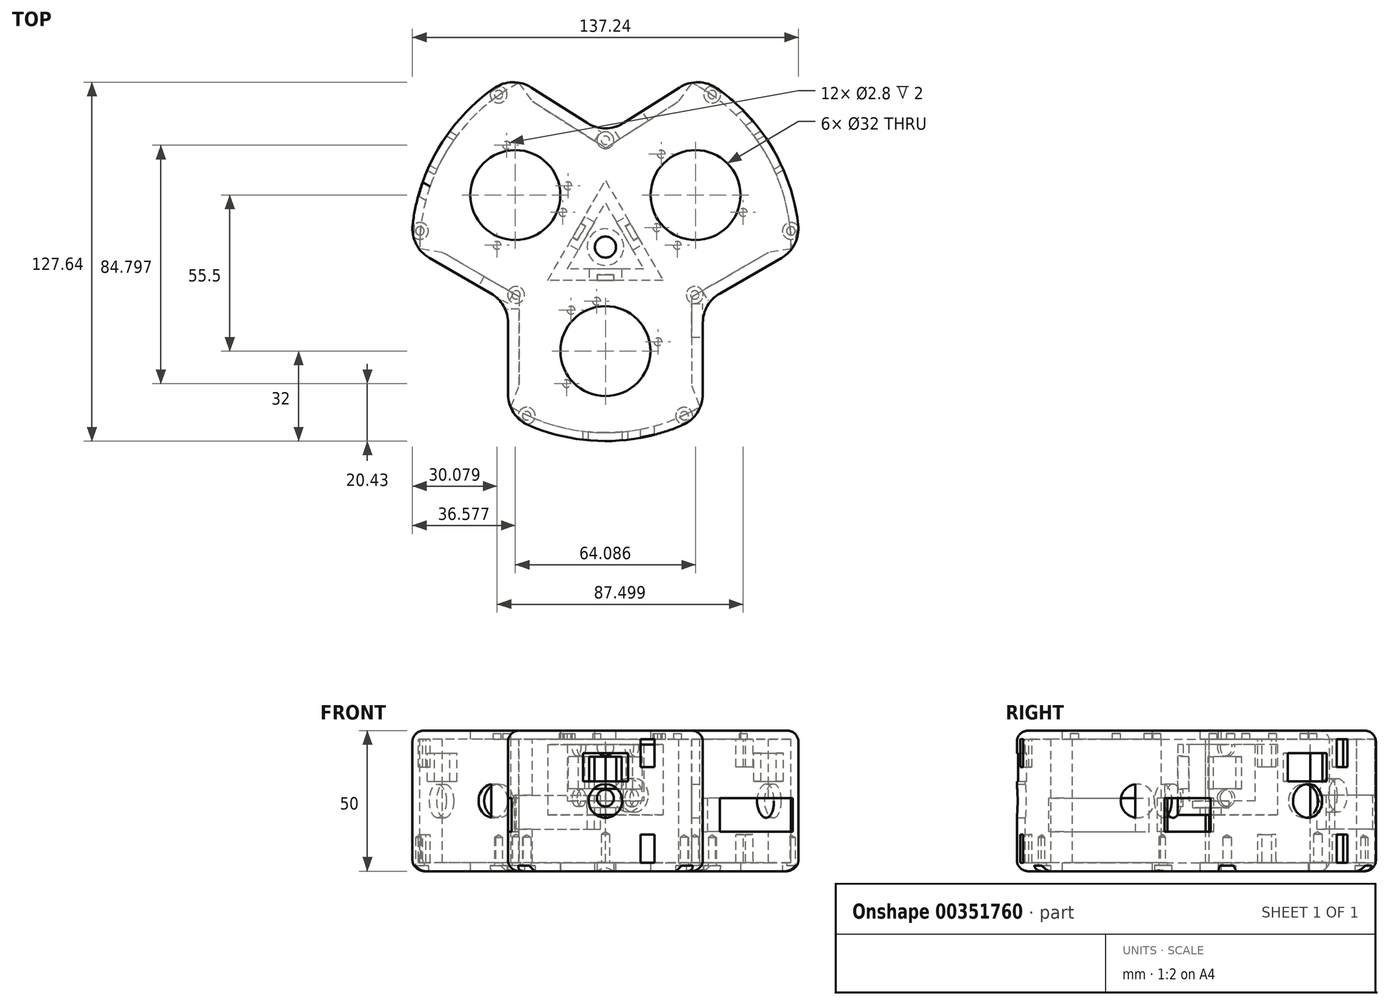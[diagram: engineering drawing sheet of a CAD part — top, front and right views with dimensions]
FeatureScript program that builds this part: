
annotation { "Feature Type Name" : "Feature", "Feature Type Description" : "" }
export const myFeature = defineFeature(function(context is Context, id is Id, definition is map)
    precondition{}
    {
        {
            var Q0;
            Q0=qCreatedBy(makeId("Top.planeOp"),FACE);
            var sketch = newSketch(context, id + "F0", { "sketchPlane" : qUnion([Q0])});
            skCircle(sketch, "E0.cCircle", {"center": v(0, 0) * mm, "radius": 7.84 * mm, "construction": true});
            skLineSegment(sketch, "E0.0", {"start": v(13.57, -7.84) * mm, "end": v(-13.57, -7.84) * mm});
            skLineSegment(sketch, "E0.1", {"start": v(-13.57, -7.84) * mm, "end": v(0, 15.67) * mm});
            skLineSegment(sketch, "E0.2", {"start": v(0, 15.67) * mm, "end": v(13.57, -7.84) * mm});
            skPoint(sketch, "E0.0.midPoint", {"position": v(0, -7.84) * mm});
            skLineSegment(sketch, "E1.0", {"start": v(-20.5, -11.84) * mm, "end": v(0, 23.67) * mm});
            skLineSegment(sketch, "E1.1", {"start": v(20.5, -11.84) * mm, "end": v(-20.5, -11.84) * mm});
            skLineSegment(sketch, "E1.2", {"start": v(0, 23.67) * mm, "end": v(20.5, -11.84) * mm});
            skCircle(sketch, "E2", {"center": v(0, 0) * mm, "radius": 3.25 * mm});
            skSolve(sketch);
        }
        {
            var Q0;
            Q0 = qSketchRegion(id + "F0", true);
            extrude(context, id + "F1", {"entities" : qUnion([Q0]), "depth" : 20 * mm, "offsetDistance" : 25 * mm});
        }
        {
            var Q0;
            Q0=makeQuery(id+"F0.imprint","IMPRINT",FACE,{"disambiguationData":[TD([[makeQuery(id+"F0.imprint","IMPRINT",EDGE,{"derivedFrom":sQuery(id+"F0.wireOp",EDGE,"E0.0")}),-1.0]])]});
            var Q1;
            Q1=makeQuery(id+"F0.imprint","IMPRINT",FACE,{"disambiguationData":[TD([[makeQuery(id+"F0.imprint","IMPRINT",EDGE,{"derivedFrom":sQuery(id+"F0.wireOp",EDGE,"E0.0")}),1.0]])]});
            var Q2;
            Q2=makeQuery(id+"F0.imprint","IMPRINT",FACE,{"disambiguationData":[TD([[makeQuery(id+"F0.imprint","IMPRINT",EDGE,{"derivedFrom":sQuery(id+"F0.wireOp",EDGE,"E2")}),1.0]])]});
            extrude(context, id + "F2", {"entities" : qUnion([Q0, Q1, Q2]), "operationType" : NewBodyOperationType.ADD, "oppositeDirection" : true, "depth" : 5 * mm, "offsetDistance" : 25 * mm});
        }
        {
            var Q0;
            {var subQ0=sQuery(id+"F0.wireOp",EDGE,"E1.1");Q0=makeQuery(id+"F2.boolean.opBoolean","MERGE",FACE,{"derivedFrom":[makeQuery(id+"F1.opExtrude","SWEPT_FACE",FACE,{"disambiguationData":[OSD([subQ0])]}),makeQuery(id+"F2.opExtrude","SWEPT_FACE",FACE,{"disambiguationData":[OSD([subQ0])]})]});}
            var sketch = newSketch(context, id + "F3", { "sketchPlane" : qUnion([Q0])});
            skLineSegment(sketch, "E3.bottom", {"start": v(5.75, 4.25) * mm, "end": v(-5.75, 4.25) * mm});
            skLineSegment(sketch, "E3.top", {"start": v(5.75, 15.75) * mm, "end": v(-5.75, 15.75) * mm});
            skLineSegment(sketch, "E3.left", {"start": v(5.75, 4.25) * mm, "end": v(5.75, 15.75) * mm});
            skLineSegment(sketch, "E3.right", {"start": v(-5.75, 4.25) * mm, "end": v(-5.75, 15.75) * mm});
            skPoint(sketch, "E3.middle", {"position": v(0, 10) * mm});
            skCircle(sketch, "E4", {"center": v(0, 10) * mm, "radius": 3.25 * mm});
            skCircle(sketch, "E5", {"center": v(0, 19) * mm, "radius": 3 * mm});
            skPoint(sketch, "E5.centerSnap0", {"position": v(0, 20) * mm});
            skCircle(sketch, "E6", {"center": v(0, 1) * mm, "radius": 3 * mm});
            skPoint(sketch, "E6.centerSnap0", {"position": v(0, 4.25) * mm});
            skSolve(sketch);
        }
        {
            var Q0;
            {var subQ0=sQuery(id+"F0.wireOp",EDGE,"E1.2");Q0=makeQuery(id+"F2.boolean.opBoolean","MERGE",FACE,{"derivedFrom":[makeQuery(id+"F1.opExtrude","SWEPT_FACE",FACE,{"disambiguationData":[OSD([subQ0])]}),makeQuery(id+"F2.opExtrude","SWEPT_FACE",FACE,{"disambiguationData":[OSD([subQ0])]})]});}
            var sketch = newSketch(context, id + "F4", { "sketchPlane" : qUnion([Q0])});
            skLineSegment(sketch, "E7.bottom", {"start": v(5.75, 4.25) * mm, "end": v(-5.75, 4.25) * mm});
            skLineSegment(sketch, "E7.top", {"start": v(5.75, 15.75) * mm, "end": v(-5.75, 15.75) * mm});
            skLineSegment(sketch, "E7.left", {"start": v(5.75, 4.25) * mm, "end": v(5.75, 15.75) * mm});
            skLineSegment(sketch, "E7.right", {"start": v(-5.75, 4.25) * mm, "end": v(-5.75, 15.75) * mm});
            skPoint(sketch, "E7.middle", {"position": v(0, 10) * mm});
            skCircle(sketch, "E8", {"center": v(0, 10) * mm, "radius": 3.25 * mm});
            skCircle(sketch, "E9", {"center": v(0, 19) * mm, "radius": 3 * mm});
            skPoint(sketch, "E9.centerSnap0", {"position": v(0, 15.75) * mm});
            skCircle(sketch, "E10", {"center": v(0, 1) * mm, "radius": 3 * mm});
            skSolve(sketch);
        }
        {
            var Q0;
            {var subQ0=sQuery(id+"F0.wireOp",EDGE,"E1.0");Q0=makeQuery(id+"F2.boolean.opBoolean","MERGE",FACE,{"derivedFrom":[makeQuery(id+"F1.opExtrude","SWEPT_FACE",FACE,{"disambiguationData":[OSD([subQ0])]}),makeQuery(id+"F2.opExtrude","SWEPT_FACE",FACE,{"disambiguationData":[OSD([subQ0])]})]});}
            var sketch = newSketch(context, id + "F5", { "sketchPlane" : qUnion([Q0])});
            skLineSegment(sketch, "E11.bottom", {"start": v(-5.75, 4.25) * mm, "end": v(5.75, 4.25) * mm});
            skLineSegment(sketch, "E11.top", {"start": v(-5.75, 15.75) * mm, "end": v(5.75, 15.75) * mm});
            skLineSegment(sketch, "E11.left", {"start": v(-5.75, 4.25) * mm, "end": v(-5.75, 15.75) * mm});
            skLineSegment(sketch, "E11.right", {"start": v(5.75, 4.25) * mm, "end": v(5.75, 15.75) * mm});
            skPoint(sketch, "E11.middle", {"position": v(0, 10) * mm});
            skCircle(sketch, "E12", {"center": v(0, 10) * mm, "radius": 3.25 * mm});
            skCircle(sketch, "E13", {"center": v(0, 19) * mm, "radius": 3 * mm});
            skPoint(sketch, "E13.centerSnap0", {"position": v(0, 15.75) * mm});
            skCircle(sketch, "E14", {"center": v(0, 1) * mm, "radius": 3 * mm});
            skPoint(sketch, "E14.centerSnap0", {"position": v(0, 4.25) * mm});
            skSolve(sketch);
        }
        {
            var Q0;
            Q0=makeQuery(id+"F5.imprint","IMPRINT",FACE,{"disambiguationData":[TD([[makeQuery(id+"F5.imprint","IMPRINT",EDGE,{"derivedFrom":sQuery(id+"F5.wireOp",EDGE,"E11.bottom")}),1.0]])]});
            extrude(context, id + "F6", {"entities" : qUnion([Q0]), "operationType" : NewBodyOperationType.REMOVE, "oppositeDirection" : true, "depth" : 7.4 * mm, "offsetDistance" : 25 * mm});
        }
        {
            var Q0;
            Q0=makeQuery(id+"F4.imprint","IMPRINT",FACE,{"disambiguationData":[TD([[makeQuery(id+"F4.imprint","IMPRINT",EDGE,{"derivedFrom":sQuery(id+"F4.wireOp",EDGE,"E7.bottom")}),-1.0]])]});
            var Q1;
            Q1=makeQuery(id+"F4.imprint","IMPRINT",FACE,{"disambiguationData":[TD([[makeQuery(id+"F4.imprint","IMPRINT",EDGE,{"derivedFrom":sQuery(id+"F4.wireOp",EDGE,"E8")}),1.0]])]});
            extrude(context, id + "F7", {"entities" : qUnion([Q0, Q1]), "operationType" : NewBodyOperationType.REMOVE, "oppositeDirection" : true, "depth" : 7.5 * mm, "offsetDistance" : 25 * mm});
        }
        {
            var Q0;
            Q0=makeQuery(id+"F3.imprint","IMPRINT",FACE,{"disambiguationData":[TD([[makeQuery(id+"F3.imprint","IMPRINT",EDGE,{"derivedFrom":sQuery(id+"F3.wireOp",EDGE,"E3.bottom")}),-1.0]])]});
            extrude(context, id + "F8", {"entities" : qUnion([Q0]), "operationType" : NewBodyOperationType.REMOVE, "oppositeDirection" : true, "depth" : 6.4 * mm, "offsetDistance" : 25 * mm});
        }
        {
            var Q0;
            Q0=makeQuery(id+"F5.imprint","IMPRINT",FACE,{"disambiguationData":[TD([[makeQuery(id+"F5.imprint","IMPRINT",EDGE,{"derivedFrom":sQuery(id+"F5.wireOp",EDGE,"E12")}),1.0]])]});
            extrude(context, id + "F9", {"entities" : qUnion([Q0]), "operationType" : NewBodyOperationType.REMOVE, "oppositeDirection" : true, "depth" : 5 * mm, "offsetDistance" : 25 * mm});
        }
        {
            var Q0;
            Q0=makeQuery(id+"F3.imprint","IMPRINT",FACE,{"disambiguationData":[TD([[makeQuery(id+"F3.imprint","IMPRINT",EDGE,{"derivedFrom":sQuery(id+"F3.wireOp",EDGE,"E4")}),1.0]])]});
            extrude(context, id + "F10", {"entities" : qUnion([Q0]), "operationType" : NewBodyOperationType.REMOVE, "oppositeDirection" : true, "depth" : 5 * mm, "offsetDistance" : 25 * mm});
        }
        {
            var Q0;
            Q0=makeQuery(id+"F4.imprint","IMPRINT",FACE,{"disambiguationData":[TD([[makeQuery(id+"F4.imprint","IMPRINT",EDGE,{"derivedFrom":sQuery(id+"F4.wireOp",EDGE,"E8")}),1.0]])]});
            extrude(context, id + "F11", {"entities" : qUnion([Q0]), "operationType" : NewBodyOperationType.REMOVE, "oppositeDirection" : true, "depth" : 5 * mm, "offsetDistance" : 25 * mm});
        }
        {
            var Q0;
            Q0=sQuery(id+"F0.wireOp",VERTEX,"E0.cCircle.center");
            var Q1;
            Q1=makeQuery(id+"F1.opExtrude","SWEPT_BODY",BODY,{"disambiguationData":[OSD([sQuery(id+"F0.wireOp",EDGE,"E0.0"),sQuery(id+"F0.wireOp",EDGE,"E0.1"),sQuery(id+"F0.wireOp",EDGE,"E0.2"),sQuery(id+"F0.wireOp",EDGE,"E1.0"),sQuery(id+"F0.wireOp",EDGE,"E1.1"),sQuery(id+"F0.wireOp",EDGE,"E1.2")])]});
            hole(context, id + "F12", {"style" : HoleStyle.C_BORE, "endStyle" : HoleEndStyle.BLIND, "holeDiameter" : 6.5 * mm, "cBoreDiameter" : 13 * mm, "cBoreDepth" : 2.5 * mm, "majorDiameter" : 5 * mm, "holeDepth" : 12 * mm, "isTappedThrough" : true, "tappedDepth" : 12 * mm, "tapClearance" : 3, "locations" : qUnion([Q0]), "scope" : qUnion([Q1])});
        }
        {
            var Q0;
            Q0=qCreatedBy(makeId("Front.planeOp"),FACE);
            var sketch = newSketch(context, id + "F13", { "sketchPlane" : qUnion([Q0])});
            skLineSegment(sketch, "E15.bottom", {"start": v(0, -22) * mm, "end": v(-66, -22) * mm});
            skLineSegment(sketch, "E15.top", {"start": v(0, 22) * mm, "end": v(-66, 22) * mm});
            skLineSegment(sketch, "E15.right", {"start": v(-66, -22) * mm, "end": v(-66, 22) * mm});
            skPoint(sketch, "E15.middle", {"position": v(-33, 0) * mm});
            skLineSegment(sketch, "E16.0", {"start": v(0, -25) * mm, "end": v(-69, -25) * mm});
            skLineSegment(sketch, "E16.1", {"start": v(-69, -25) * mm, "end": v(-69, 25) * mm});
            skLineSegment(sketch, "E16.2", {"start": v(0, 25) * mm, "end": v(-69, 25) * mm});
            skLineSegment(sketch, "E17", {"start": v(0, 25) * mm, "end": v(0, 22) * mm});
            skLineSegment(sketch, "E18", {"start": v(0, -22) * mm, "end": v(0, -25) * mm});
            skLineSegment(sketch, "E19", {"start": v(-66, -22) * mm, "end": v(-69, -22) * mm});
            skSolve(sketch);
        }
        {
            var Q0;
            Q0=makeQuery(id+"F13.imprint","IMPRINT",FACE,{"disambiguationData":[TD([[makeQuery(id+"F13.imprint","IMPRINT",EDGE,{"derivedFrom":sQuery(id+"F13.wireOp",EDGE,"E15.top")}),-1.0]])]});
            var Q1;
            Q1=sQuery(id+"F13.wireOp",EDGE,"E17");
            revolve(context, id + "F14", {"entities" : qUnion([Q0]), "axis" : qUnion([Q1]), "revolveType" : RevolveType.FULL, "surfaceOperationType" : NewSurfaceOperationType.NEW});
        }
        {
            var Q0;
            Q0=makeQuery(id+"F13.imprint","IMPRINT",FACE,{"disambiguationData":[TD([[makeQuery(id+"F13.imprint","IMPRINT",EDGE,{"derivedFrom":sQuery(id+"F13.wireOp",EDGE,"E15.bottom")}),1.0]])]});
            var Q1;
            Q1=sQuery(id+"F13.wireOp",EDGE,"E18");
            revolve(context, id + "F15", {"surfaceOperationType" : NewSurfaceOperationType.NEW, "entities" : qUnion([Q0]), "axis" : qUnion([Q1]), "revolveType" : RevolveType.FULL});
        }
        {
            var Q0;
            Q0=qCreatedBy(makeId("Top.planeOp"),FACE);
            var sketch = newSketch(context, id + "F16", { "sketchPlane" : qUnion([Q0])});
            skCircle(sketch, "E20", {"center": v(0, -37) * mm, "radius": 16 * mm});
            skLineSegment(sketch, "E21", {"start": v(48.46, 27.98) * mm, "end": v(0, 0) * mm, "construction": true});
            skLineSegment(sketch, "E22", {"start": v(0, 0) * mm, "end": v(-43.02, 24.84) * mm, "construction": true});
            skCircle(sketch, "E23", {"center": v(32.04, 18.5) * mm, "radius": 16 * mm});
            skCircle(sketch, "E24", {"center": v(-32.04, 18.5) * mm, "radius": 16 * mm});
            skCircle(sketch, "E25", {"center": v(0, 0) * mm, "radius": 3.25 * mm});
            skSolve(sketch);
        }
        {
            var Q0;
            Q0=makeQuery(id+"F16.imprint","IMPRINT",FACE,{"disambiguationData":[TD([[makeQuery(id+"F16.imprint","IMPRINT",EDGE,{"derivedFrom":sQuery(id+"F16.wireOp",EDGE,"E24")}),1.0]])]});
            var Q1;
            Q1=makeQuery(id+"F16.imprint","IMPRINT",FACE,{"disambiguationData":[TD([[makeQuery(id+"F16.imprint","IMPRINT",EDGE,{"derivedFrom":sQuery(id+"F16.wireOp",EDGE,"E23")}),1.0]])]});
            var Q2;
            Q2=makeQuery(id+"F16.imprint","IMPRINT",FACE,{"disambiguationData":[TD([[makeQuery(id+"F16.imprint","IMPRINT",EDGE,{"derivedFrom":sQuery(id+"F16.wireOp",EDGE,"E20")}),1.0]])]});
            extrude(context, id + "F17", {"entities" : qUnion([Q0, Q1, Q2]), "operationType" : NewBodyOperationType.REMOVE, "depth" : 64 * mm, "offsetDistance" : 25 * mm, "hasSecondDirection" : true, "secondDirectionOppositeDirection" : true, "secondDirectionDepth" : 43 * mm});
        }
        {
            var Q0;
            Q0=qCreatedBy(makeId("Front.planeOp"),FACE);
            var sketch = newSketch(context, id + "F18", { "sketchPlane" : qUnion([Q0])});
            skLineSegment(sketch, "E26.bottom", {"start": v(8, 7) * mm, "end": v(-8, 7) * mm});
            skLineSegment(sketch, "E26.top", {"start": v(8, 17) * mm, "end": v(-8, 17) * mm});
            skLineSegment(sketch, "E26.left", {"start": v(8, 7) * mm, "end": v(8, 17) * mm});
            skLineSegment(sketch, "E26.right", {"start": v(-8, 7) * mm, "end": v(-8, 17) * mm});
            skPoint(sketch, "E26.middle", {"position": v(0, 12) * mm});
            skCircle(sketch, "E27", {"center": v(0, 0) * mm, "radius": 6 * mm});
            skLineSegment(sketch, "E28.bottom", {"start": v(17.5, 12) * mm, "end": v(12.5, 12) * mm});
            skLineSegment(sketch, "E28.top", {"start": v(17.5, 22) * mm, "end": v(12.5, 22) * mm});
            skLineSegment(sketch, "E28.left", {"start": v(17.5, 12) * mm, "end": v(17.5, 22) * mm});
            skLineSegment(sketch, "E28.right", {"start": v(12.5, 12) * mm, "end": v(12.5, 22) * mm});
            skPoint(sketch, "E28.middle", {"position": v(15, 17) * mm});
            skLineSegment(sketch, "E29.bottom", {"start": v(17.5, -22) * mm, "end": v(12.5, -22) * mm});
            skLineSegment(sketch, "E29.top", {"start": v(17.5, -12) * mm, "end": v(12.5, -12) * mm});
            skLineSegment(sketch, "E29.left", {"start": v(17.5, -22) * mm, "end": v(17.5, -12) * mm});
            skLineSegment(sketch, "E29.right", {"start": v(12.5, -22) * mm, "end": v(12.5, -12) * mm});
            skPoint(sketch, "E29.middle", {"position": v(15, -17) * mm});
            skPoint(sketch, "E29.cornerSnap0", {"position": v(17.5, 17) * mm});
            skSolve(sketch);
        }
        {
            var Q0;
            Q0 = qSketchRegion(id + "F18", true);
            extrude(context, id + "F19", {"entities" : qUnion([Q0]), "operationType" : NewBodyOperationType.REMOVE, "depth" : 101.5 * mm, "offsetDistance" : 25 * mm, "hasSecondDirection" : true, "secondDirectionOppositeDirection" : false, "secondDirectionDepth" : 60 * mm});
        }
        {
            var Q0;
            {var subQ0=sQuery(id+"F0.wireOp",EDGE,"E1.2");var subQ1=sQuery(id+"F0.wireOp",EDGE,"E1.1");Q0=makeQuery(id+"F2.boolean.opBoolean","MERGE",EDGE,{"derivedFrom":[makeQuery(id+"F1.opExtrude","SWEPT_EDGE",EDGE,{"disambiguationData":[OSD([subQ1,subQ0])]}),makeQuery(id+"F2.opExtrude","SWEPT_EDGE",EDGE,{"disambiguationData":[OSD([subQ1,subQ0])]})]});}
            cPlane(context, id + "F20", {"entities" : qUnion([Q0]), "cplaneType" : CPlaneType.LINE_ANGLE, "offset" : 134 * mm, "angle" : 30 * degree, "width" : 150 * mm, "height" : 150 * mm});
        }
        {
            var Q0;
            {var subQ0=sQuery(id+"F0.wireOp",EDGE,"E1.1");var subQ1=sQuery(id+"F0.wireOp",EDGE,"E1.0");Q0=makeQuery(id+"F2.boolean.opBoolean","MERGE",EDGE,{"derivedFrom":[makeQuery(id+"F1.opExtrude","SWEPT_EDGE",EDGE,{"disambiguationData":[OSD([subQ1,subQ0])]}),makeQuery(id+"F2.opExtrude","SWEPT_EDGE",EDGE,{"disambiguationData":[OSD([subQ1,subQ0])]})]});}
            cPlane(context, id + "F21", {"entities" : qUnion([Q0]), "cplaneType" : CPlaneType.LINE_ANGLE, "offset" : 25 * mm, "angle" : 30 * degree, "oppositeDirection" : true, "width" : 150 * mm, "height" : 150 * mm});
        }
        {
            var Q0;
            Q0=qCreatedBy(id+"F21.planeOp",FACE);
            var sketch = newSketch(context, id + "F22", { "sketchPlane" : qUnion([Q0])});
            skLineSegment(sketch, "E30.bottom", {"start": v(-8, 7) * mm, "end": v(8, 7) * mm});
            skLineSegment(sketch, "E30.top", {"start": v(-8, 17) * mm, "end": v(8, 17) * mm});
            skLineSegment(sketch, "E30.left", {"start": v(-8, 7) * mm, "end": v(-8, 17) * mm});
            skLineSegment(sketch, "E30.right", {"start": v(8, 7) * mm, "end": v(8, 17) * mm});
            skPoint(sketch, "E30.middle", {"position": v(0, 12) * mm});
            skCircle(sketch, "E31", {"center": v(0, 0) * mm, "radius": 6 * mm});
            skLineSegment(sketch, "E32.bottom", {"start": v(-12.5, 12) * mm, "end": v(-17.5, 12) * mm});
            skLineSegment(sketch, "E32.top", {"start": v(-12.5, 22) * mm, "end": v(-17.5, 22) * mm});
            skLineSegment(sketch, "E32.left", {"start": v(-12.5, 12) * mm, "end": v(-12.5, 22) * mm});
            skLineSegment(sketch, "E32.right", {"start": v(-17.5, 12) * mm, "end": v(-17.5, 22) * mm});
            skPoint(sketch, "E32.middle", {"position": v(-15, 17) * mm});
            skLineSegment(sketch, "E33.bottom", {"start": v(-17.5, -22) * mm, "end": v(-12.5, -22) * mm});
            skLineSegment(sketch, "E33.top", {"start": v(-17.5, -12) * mm, "end": v(-12.5, -12) * mm});
            skLineSegment(sketch, "E33.left", {"start": v(-17.5, -22) * mm, "end": v(-17.5, -12) * mm});
            skLineSegment(sketch, "E33.right", {"start": v(-12.5, -22) * mm, "end": v(-12.5, -12) * mm});
            skPoint(sketch, "E33.middle", {"position": v(-15, -17) * mm});
            skPoint(sketch, "E33.middle.positionSnap0", {"position": v(-15, 12) * mm});
            skPoint(sketch, "E33.centerSnap0", {"position": v(-15, 12) * mm});
            skSolve(sketch);
        }
        {
            var Q0;
            Q0 = qSketchRegion(id + "F22", true);
            extrude(context, id + "F23", {"entities" : qUnion([Q0]), "operationType" : NewBodyOperationType.REMOVE, "oppositeDirection" : true, "depth" : 107 * mm, "offsetDistance" : 25 * mm, "hasSecondDirection" : true, "secondDirectionOppositeDirection" : true, "secondDirectionDepth" : 84 * mm});
        }
        {
            var Q0;
            Q0=qCreatedBy(id+"F20.planeOp",FACE);
            var sketch = newSketch(context, id + "F24", { "sketchPlane" : qUnion([Q0])});
            skLineSegment(sketch, "E34.bottom", {"start": v(8, 7) * mm, "end": v(-8, 7) * mm});
            skLineSegment(sketch, "E34.top", {"start": v(8, 17) * mm, "end": v(-8, 17) * mm});
            skLineSegment(sketch, "E34.left", {"start": v(8, 7) * mm, "end": v(8, 17) * mm});
            skLineSegment(sketch, "E34.right", {"start": v(-8, 7) * mm, "end": v(-8, 17) * mm});
            skPoint(sketch, "E34.middle", {"position": v(0, 12) * mm});
            skPoint(sketch, "E35.centerSnap0", {"position": v(0, 7) * mm});
            skCircle(sketch, "E36", {"center": v(0, 0) * mm, "radius": 6 * mm});
            skLineSegment(sketch, "E37.bottom", {"start": v(12.5, 12) * mm, "end": v(17.5, 12) * mm});
            skLineSegment(sketch, "E37.top", {"start": v(12.5, 22) * mm, "end": v(17.5, 22) * mm});
            skLineSegment(sketch, "E37.left", {"start": v(12.5, 12) * mm, "end": v(12.5, 22) * mm});
            skLineSegment(sketch, "E37.right", {"start": v(17.5, 12) * mm, "end": v(17.5, 22) * mm});
            skPoint(sketch, "E37.middle", {"position": v(15, 17) * mm});
            skLineSegment(sketch, "E38.bottom", {"start": v(17.5, -22) * mm, "end": v(12.5, -22) * mm});
            skLineSegment(sketch, "E38.top", {"start": v(17.5, -12) * mm, "end": v(12.5, -12) * mm});
            skLineSegment(sketch, "E38.left", {"start": v(17.5, -22) * mm, "end": v(17.5, -12) * mm});
            skLineSegment(sketch, "E38.right", {"start": v(12.5, -22) * mm, "end": v(12.5, -12) * mm});
            skPoint(sketch, "E38.middle", {"position": v(15, -17) * mm});
            skPoint(sketch, "E38.cornerSnap0", {"position": v(17.5, 17) * mm});
            skSolve(sketch);
        }
        {
            var Q0;
            Q0 = qSketchRegion(id + "F24", true);
            extrude(context, id + "F25", {"entities" : qUnion([Q0]), "operationType" : NewBodyOperationType.REMOVE, "depth" : 108.4 * mm, "offsetDistance" : 25 * mm, "hasSecondDirection" : true, "secondDirectionOppositeDirection" : false, "secondDirectionDepth" : 81.1 * mm});
        }
        {
            var Q0;
            Q0=qCreatedBy(makeId("Top.planeOp"),FACE);
            var sketch = newSketch(context, id + "F26", { "sketchPlane" : qUnion([Q0])});
            skCircle(sketch, "E39", {"center": v(0, 0) * mm, "radius": 3.75 * mm});
            skSolve(sketch);
        }
        {
            var Q0;
            Q0 = qSketchRegion(id + "F26", true);
            extrude(context, id + "F27", {"entities" : qUnion([Q0]), "operationType" : NewBodyOperationType.REMOVE, "oppositeDirection" : true, "depth" : 25 * mm, "offsetDistance" : 25 * mm, "hasSecondDirection" : true, "secondDirectionOppositeDirection" : false, "secondDirectionDepth" : 43 * mm});
        }
        {
            var Q0;
            Q0=qCreatedBy(makeId("Right.planeOp"),FACE);
            var sketch = newSketch(context, id + "F28", { "sketchPlane" : qUnion([Q0])});
            skLineSegment(sketch, "E40.bottom", {"start": v(100, -26) * mm, "end": v(40, -26) * mm});
            skLineSegment(sketch, "E40.top", {"start": v(100, 26) * mm, "end": v(40, 26) * mm});
            skLineSegment(sketch, "E40.left", {"start": v(40, -26) * mm, "end": v(40, 26) * mm});
            skLineSegment(sketch, "E40.right", {"start": v(100, -26) * mm, "end": v(100, 26) * mm});
            skPoint(sketch, "E40.middle", {"position": v(70, 0) * mm});
            skSolve(sketch);
        }
        {
            var Q0;
            Q0=makeQuery(id+"F28.imprint","IMPRINT",FACE,{"disambiguationData":[TD([[makeQuery(id+"F28.imprint","IMPRINT",EDGE,{"derivedFrom":sQuery(id+"F28.wireOp",EDGE,"E40.bottom")}),-1.0]])]});
            var Q1;
            Q1=sQuery(id+"F28.wireOp",EDGE,"E40.left");
            revolve(context, id + "F29", {"operationType" : NewBodyOperationType.REMOVE, "surfaceOperationType" : NewSurfaceOperationType.NEW, "entities" : qUnion([Q0]), "axis" : qUnion([Q1]), "revolveType" : RevolveType.SYMMETRIC, "angle" : 115 * degree});
        }
        {
            var Q0;
            {var subQ0=sQuery(id+"F0.wireOp",EDGE,"E1.1");var subQ1=sQuery(id+"F0.wireOp",EDGE,"E1.0");Q0=makeQuery(id+"F2.boolean.opBoolean","MERGE",EDGE,{"derivedFrom":[makeQuery(id+"F1.opExtrude","SWEPT_EDGE",EDGE,{"disambiguationData":[OSD([subQ1,subQ0])]}),makeQuery(id+"F2.opExtrude","SWEPT_EDGE",EDGE,{"disambiguationData":[OSD([subQ1,subQ0])]})]});}
            cPlane(context, id + "F30", {"entities" : qUnion([Q0]), "cplaneType" : CPlaneType.LINE_ANGLE, "offset" : 25 * mm, "angle" : 60 * degree, "width" : 150 * mm, "height" : 150 * mm});
        }
        {
            var Q0;
            {var subQ0=sQuery(id+"F0.wireOp",EDGE,"E1.2");var subQ1=sQuery(id+"F0.wireOp",EDGE,"E1.1");Q0=makeQuery(id+"F2.boolean.opBoolean","MERGE",EDGE,{"derivedFrom":[makeQuery(id+"F1.opExtrude","SWEPT_EDGE",EDGE,{"disambiguationData":[OSD([subQ1,subQ0])]}),makeQuery(id+"F2.opExtrude","SWEPT_EDGE",EDGE,{"disambiguationData":[OSD([subQ1,subQ0])]})]});}
            cPlane(context, id + "F31", {"entities" : qUnion([Q0]), "cplaneType" : CPlaneType.LINE_ANGLE, "offset" : 25 * mm, "angle" : 60 * degree, "oppositeDirection" : true, "width" : 150 * mm, "height" : 150 * mm});
        }
        {
            var Q0;
            Q0=qCreatedBy(id+"F30.planeOp",FACE);
            var sketch = newSketch(context, id + "F32", { "sketchPlane" : qUnion([Q0])});
            skLineSegment(sketch, "E41.bottom", {"start": v(100, 40) * mm, "end": v(40, 40) * mm});
            skLineSegment(sketch, "E41.top", {"start": v(100, -40) * mm, "end": v(40, -40) * mm});
            skLineSegment(sketch, "E41.left", {"start": v(100, 40) * mm, "end": v(100, -40) * mm});
            skLineSegment(sketch, "E41.right", {"start": v(40, 40) * mm, "end": v(40, -40) * mm});
            skPoint(sketch, "E41.middle", {"position": v(70, 0) * mm});
            skSolve(sketch);
        }
        {
            var Q0;
            Q0=makeQuery(id+"F32.imprint","IMPRINT",FACE,{"disambiguationData":[TD([[makeQuery(id+"F32.imprint","IMPRINT",EDGE,{"derivedFrom":sQuery(id+"F32.wireOp",EDGE,"E41.bottom")}),1.0]])]});
            var Q1;
            Q1=sQuery(id+"F32.wireOp",EDGE,"E41.right");
            revolve(context, id + "F33", {"operationType" : NewBodyOperationType.REMOVE, "surfaceOperationType" : NewSurfaceOperationType.NEW, "entities" : qUnion([Q0]), "axis" : qUnion([Q1]), "revolveType" : RevolveType.SYMMETRIC, "oppositeDirection" : true, "angle" : 120 * degree});
        }
        {
            var Q0;
            Q0=qCreatedBy(id+"F31.planeOp",FACE);
            var sketch = newSketch(context, id + "F34", { "sketchPlane" : qUnion([Q0])});
            skLineSegment(sketch, "E42.bottom", {"start": v(188.45, 46.08) * mm, "end": v(40, 46.08) * mm});
            skLineSegment(sketch, "E42.top", {"start": v(188.45, -46.08) * mm, "end": v(40, -46.08) * mm});
            skLineSegment(sketch, "E42.left", {"start": v(188.45, 46.08) * mm, "end": v(188.45, -46.08) * mm});
            skLineSegment(sketch, "E42.right", {"start": v(40, 46.08) * mm, "end": v(40, -46.08) * mm});
            skPoint(sketch, "E42.middle", {"position": v(114.22, 0) * mm});
            skSolve(sketch);
        }
        {
            var Q0;
            Q0=makeQuery(id+"F34.imprint","IMPRINT",FACE,{"disambiguationData":[TD([[makeQuery(id+"F34.imprint","IMPRINT",EDGE,{"derivedFrom":sQuery(id+"F34.wireOp",EDGE,"E42.bottom")}),1.0]])]});
            var Q1;
            Q1=sQuery(id+"F34.wireOp",EDGE,"E42.right");
            revolve(context, id + "F35", {"operationType" : NewBodyOperationType.REMOVE, "surfaceOperationType" : NewSurfaceOperationType.NEW, "entities" : qUnion([Q0]), "axis" : qUnion([Q1]), "revolveType" : RevolveType.SYMMETRIC, "oppositeDirection" : true, "angle" : 120 * degree});
        }
        {
            var Q0;
            Q0=makeQuery(id+"F14.opRevolve","SWEPT_FACE",FACE,{"disambiguationData":[OSD([sQuery(id+"F13.wireOp",EDGE,"E16.2")])]});
            var sketch = newSketch(context, id + "F36", { "sketchPlane" : qUnion([Q0])});
            skLineSegment(sketch, "E43.0", {"start": v(30.64, -17.7) * mm, "end": v(30.64, -49.25) * mm});
            skLineSegment(sketch, "E43.2", {"start": v(30.64, -17.7) * mm, "end": v(57.97, -1.91) * mm});
            skLineSegment(sketch, "E43.3", {"start": v(-30.64, -17.7) * mm, "end": v(-30.64, -49.25) * mm});
            skLineSegment(sketch, "E43.4", {"start": v(-30.64, -17.7) * mm, "end": v(-57.97, -1.91) * mm});
            skLineSegment(sketch, "E43.6", {"start": v(0, 35.26) * mm, "end": v(26.02, 51.83) * mm});
            skLineSegment(sketch, "E43.7", {"start": v(0, 35.26) * mm, "end": v(-26.02, 51.83) * mm});
            skLineSegment(sketch, "E44", {"start": v(57.97, -1.91) * mm, "end": v(69, -0.16) * mm});
            skLineSegment(sketch, "E45", {"start": v(30.64, -49.25) * mm, "end": v(34.64, -59.67) * mm});
            skLineSegment(sketch, "E46", {"start": v(-30.64, -49.25) * mm, "end": v(-34.64, -59.67) * mm});
            skLineSegment(sketch, "E47", {"start": v(-57.97, -1.91) * mm, "end": v(-69, -0.16) * mm});
            skLineSegment(sketch, "E48", {"start": v(-26.02, 51.83) * mm, "end": v(-32.64, 60.8) * mm});
            skLineSegment(sketch, "E49", {"start": v(26.02, 51.83) * mm, "end": v(32.64, 60.8) * mm});
            skSolve(sketch);
        }
        {
            var Q0;
            Q0=makeQuery(id+"F36.imprint","IMPRINT",FACE,{"disambiguationData":[TD([[makeQuery(id+"F36.imprint","IMPRINT",EDGE,{"derivedFrom":sQuery(id+"F36.wireOp",EDGE,"E43.6")}),1.0]])]});
            var Q1;
            Q1=makeQuery(id+"F36.imprint","IMPRINT",FACE,{"disambiguationData":[TD([[makeQuery(id+"F36.imprint","IMPRINT",EDGE,{"derivedFrom":sQuery(id+"F36.wireOp",EDGE,"E43.0")}),1.0]])]});
            var Q2;
            Q2=makeQuery(id+"F36.imprint","IMPRINT",FACE,{"disambiguationData":[TD([[makeQuery(id+"F36.imprint","IMPRINT",EDGE,{"derivedFrom":sQuery(id+"F36.wireOp",EDGE,"E43.3")}),-1.0]])]});
            extrude(context, id + "F37", {"entities" : qUnion([Q0, Q1, Q2]), "operationType" : NewBodyOperationType.ADD, "oppositeDirection" : true, "depth" : 47 * mm, "offsetDistance" : 25 * mm});
        }
        {
            var Q0;
            Q0=makeQuery(id+"F33.boolean.opBoolean","INTERSECT",EDGE,{"derivedFrom":[makeQuery(id+"F14.opRevolve","SWEPT_FACE",FACE,{"disambiguationData":[OSD([sQuery(id+"F13.wireOp",EDGE,"E16.1")])]}),makeQuery(id+"F33.opRevolve","CAP_FACE",FACE,{"disambiguationData":[OSD([sQuery(id+"F32.wireOp",EDGE,"E41.bottom"),sQuery(id+"F32.wireOp",EDGE,"E41.top"),sQuery(id+"F32.wireOp",EDGE,"E41.left"),sQuery(id+"F32.wireOp",EDGE,"E41.right")])],"isStart":true})]});
            var Q1;
            Q1=makeQuery(id+"F33.boolean.opBoolean","INTERSECT",EDGE,{"derivedFrom":[makeQuery(id+"F14.opRevolve","SWEPT_FACE",FACE,{"disambiguationData":[OSD([sQuery(id+"F13.wireOp",EDGE,"E16.1")])]}),makeQuery(id+"F33.opRevolve","CAP_FACE",FACE,{"disambiguationData":[OSD([sQuery(id+"F32.wireOp",EDGE,"E41.bottom"),sQuery(id+"F32.wireOp",EDGE,"E41.top"),sQuery(id+"F32.wireOp",EDGE,"E41.left"),sQuery(id+"F32.wireOp",EDGE,"E41.right")])],"isStart":false})]});
            var Q2;
            {var subQ0=sQuery(id+"F32.wireOp",EDGE,"E41.right");var subQ1=sQuery(id+"F32.wireOp",EDGE,"E41.left");var subQ2=sQuery(id+"F32.wireOp",EDGE,"E41.top");var subQ3=sQuery(id+"F32.wireOp",EDGE,"E41.bottom");var subQ4=sQuery(id+"F13.wireOp",EDGE,"E16.2");Q2=makeQuery(id+"F37.boolean.opBoolean","MERGE",EDGE,{"derivedFrom":[makeQuery(id+"F33.boolean.opBoolean","COPY",EDGE,{"disambiguationData":[TD([makeQuery(id+"F14.opRevolve","SWEPT_FACE",FACE,{"disambiguationData":[OSD([sQuery(id+"F13.wireOp",EDGE,"E15.top")])]})])],"derivedFrom":makeQuery(id+"F33.opRevolve","CAP_EDGE",EDGE,{"disambiguationData":[OSD([subQ0])],"isStart":true})}),makeQuery(id+"F37.opExtrude","SWEPT_EDGE",EDGE,{"disambiguationData":[OSD([subQ4,subQ3,subQ2,subQ1,subQ0])]})]});}
            var Q3;
            {var subQ1=makeQuery(id+"F14.opRevolve","SWEPT_FACE",FACE,{"disambiguationData":[OSD([sQuery(id+"F13.wireOp",EDGE,"E16.1")])]});Q3=makeQuery(id+"F35.boolean.opBoolean","INTERSECT",EDGE,{"derivedFrom":[makeQuery(id+"F33.boolean.opBoolean","SPLIT",FACE,{"disambiguationData":[TD([makeQuery(id+"F19.boolean.opBoolean","COPY",FACE,{"derivedFrom":makeQuery(id+"F19.opExtrude","SWEPT_FACE",FACE,{"disambiguationData":[OSD([sQuery(id+"F18.wireOp",EDGE,"E26.bottom")])]})})])],"derivedFrom":subQ1}),makeQuery(id+"F35.opRevolve","CAP_FACE",FACE,{"disambiguationData":[OSD([sQuery(id+"F34.wireOp",EDGE,"E42.bottom"),sQuery(id+"F34.wireOp",EDGE,"E42.top"),sQuery(id+"F34.wireOp",EDGE,"E42.left"),sQuery(id+"F34.wireOp",EDGE,"E42.right")])],"isStart":true})]});}
            var Q4;
            {var subQ0=sQuery(id+"F34.wireOp",EDGE,"E42.right");var subQ1=sQuery(id+"F34.wireOp",EDGE,"E42.left");var subQ2=sQuery(id+"F34.wireOp",EDGE,"E42.top");var subQ3=sQuery(id+"F34.wireOp",EDGE,"E42.bottom");var subQ4=sQuery(id+"F13.wireOp",EDGE,"E16.2");Q4=makeQuery(id+"F37.boolean.opBoolean","MERGE",EDGE,{"derivedFrom":[makeQuery(id+"F35.boolean.opBoolean","COPY",EDGE,{"disambiguationData":[TD([makeQuery(id+"F14.opRevolve","SWEPT_FACE",FACE,{"disambiguationData":[OSD([sQuery(id+"F13.wireOp",EDGE,"E15.top")])]})])],"derivedFrom":makeQuery(id+"F35.opRevolve","CAP_EDGE",EDGE,{"disambiguationData":[OSD([subQ0])],"isStart":true})}),makeQuery(id+"F37.opExtrude","SWEPT_EDGE",EDGE,{"disambiguationData":[OSD([subQ4,subQ3,subQ2,subQ1,subQ0])]})]});}
            var Q5;
            Q5=makeQuery(id+"F29.boolean.opBoolean","INTERSECT",EDGE,{"derivedFrom":[makeQuery(id+"F14.opRevolve","SWEPT_FACE",FACE,{"disambiguationData":[OSD([sQuery(id+"F13.wireOp",EDGE,"E16.1")])]}),makeQuery(id+"F29.opRevolve","CAP_FACE",FACE,{"disambiguationData":[OSD([sQuery(id+"F28.wireOp",EDGE,"E40.bottom"),sQuery(id+"F28.wireOp",EDGE,"E40.top"),sQuery(id+"F28.wireOp",EDGE,"E40.left"),sQuery(id+"F28.wireOp",EDGE,"E40.right")])],"isStart":true})]});
            var Q6;
            Q6=makeQuery(id+"F29.boolean.opBoolean","INTERSECT",EDGE,{"derivedFrom":[makeQuery(id+"F14.opRevolve","SWEPT_FACE",FACE,{"disambiguationData":[OSD([sQuery(id+"F13.wireOp",EDGE,"E16.1")])]}),makeQuery(id+"F29.opRevolve","CAP_FACE",FACE,{"disambiguationData":[OSD([sQuery(id+"F28.wireOp",EDGE,"E40.bottom"),sQuery(id+"F28.wireOp",EDGE,"E40.top"),sQuery(id+"F28.wireOp",EDGE,"E40.left"),sQuery(id+"F28.wireOp",EDGE,"E40.right")])],"isStart":false})]});
            var Q7;
            Q7=makeQuery(id+"F33.boolean.opBoolean","INTERSECT",EDGE,{"derivedFrom":[makeQuery(id+"F15.opRevolve","SWEPT_FACE",FACE,{"disambiguationData":[OSD([sQuery(id+"F13.wireOp",EDGE,"E16.1")])]}),makeQuery(id+"F33.opRevolve","CAP_FACE",FACE,{"disambiguationData":[OSD([sQuery(id+"F32.wireOp",EDGE,"E41.bottom"),sQuery(id+"F32.wireOp",EDGE,"E41.top"),sQuery(id+"F32.wireOp",EDGE,"E41.left"),sQuery(id+"F32.wireOp",EDGE,"E41.right")])],"isStart":true})]});
            var Q8;
            Q8=makeQuery(id+"F33.boolean.opBoolean","INTERSECT",EDGE,{"derivedFrom":[makeQuery(id+"F15.opRevolve","SWEPT_FACE",FACE,{"disambiguationData":[OSD([sQuery(id+"F13.wireOp",EDGE,"E16.1")])]}),makeQuery(id+"F33.opRevolve","CAP_FACE",FACE,{"disambiguationData":[OSD([sQuery(id+"F32.wireOp",EDGE,"E41.bottom"),sQuery(id+"F32.wireOp",EDGE,"E41.top"),sQuery(id+"F32.wireOp",EDGE,"E41.left"),sQuery(id+"F32.wireOp",EDGE,"E41.right")])],"isStart":false})]});
            var Q9;
            {var subQ0=sQuery(id+"F32.wireOp",EDGE,"E41.right");Q9=makeQuery(id+"F33.boolean.opBoolean","COPY",EDGE,{"disambiguationData":[TD([makeQuery(id+"F15.opRevolve","SWEPT_FACE",FACE,{"disambiguationData":[OSD([sQuery(id+"F13.wireOp",EDGE,"E16.0")])]})])],"derivedFrom":makeQuery(id+"F33.opRevolve","CAP_EDGE",EDGE,{"disambiguationData":[OSD([subQ0])],"isStart":true})});}
            var Q10;
            {var subQ2=makeQuery(id+"F15.opRevolve","SWEPT_FACE",FACE,{"disambiguationData":[OSD([sQuery(id+"F13.wireOp",EDGE,"E16.1")])]});Q10=makeQuery(id+"F35.boolean.opBoolean","INTERSECT",EDGE,{"derivedFrom":[makeQuery(id+"F33.boolean.opBoolean","SPLIT",FACE,{"disambiguationData":[TD([makeQuery(id+"F33.opRevolve","CAP_FACE",FACE,{"disambiguationData":[OSD([sQuery(id+"F32.wireOp",EDGE,"E41.bottom"),sQuery(id+"F32.wireOp",EDGE,"E41.top"),sQuery(id+"F32.wireOp",EDGE,"E41.left"),sQuery(id+"F32.wireOp",EDGE,"E41.right")])],"isStart":false})])],"derivedFrom":subQ2}),makeQuery(id+"F35.opRevolve","CAP_FACE",FACE,{"disambiguationData":[OSD([sQuery(id+"F34.wireOp",EDGE,"E42.bottom"),sQuery(id+"F34.wireOp",EDGE,"E42.top"),sQuery(id+"F34.wireOp",EDGE,"E42.left"),sQuery(id+"F34.wireOp",EDGE,"E42.right")])],"isStart":true})]});}
            var Q11;
            {var subQ0=sQuery(id+"F34.wireOp",EDGE,"E42.right");Q11=makeQuery(id+"F35.boolean.opBoolean","COPY",EDGE,{"disambiguationData":[TD([makeQuery(id+"F15.opRevolve","SWEPT_FACE",FACE,{"disambiguationData":[OSD([sQuery(id+"F13.wireOp",EDGE,"E16.0")])]})])],"derivedFrom":makeQuery(id+"F35.opRevolve","CAP_EDGE",EDGE,{"disambiguationData":[OSD([subQ0])],"isStart":true})});}
            var Q12;
            {var subQ2=makeQuery(id+"F15.opRevolve","SWEPT_FACE",FACE,{"disambiguationData":[OSD([sQuery(id+"F13.wireOp",EDGE,"E16.1")])]});Q12=makeQuery(id+"F35.boolean.opBoolean","INTERSECT",EDGE,{"derivedFrom":[makeQuery(id+"F33.boolean.opBoolean","SPLIT",FACE,{"disambiguationData":[TD([makeQuery(id+"F33.opRevolve","CAP_FACE",FACE,{"disambiguationData":[OSD([sQuery(id+"F32.wireOp",EDGE,"E41.bottom"),sQuery(id+"F32.wireOp",EDGE,"E41.top"),sQuery(id+"F32.wireOp",EDGE,"E41.left"),sQuery(id+"F32.wireOp",EDGE,"E41.right")])],"isStart":false})])],"derivedFrom":subQ2}),makeQuery(id+"F35.opRevolve","CAP_FACE",FACE,{"disambiguationData":[OSD([sQuery(id+"F34.wireOp",EDGE,"E42.bottom"),sQuery(id+"F34.wireOp",EDGE,"E42.top"),sQuery(id+"F34.wireOp",EDGE,"E42.left"),sQuery(id+"F34.wireOp",EDGE,"E42.right")])],"isStart":false})]});}
            var Q13;
            Q13=makeQuery(id+"F29.boolean.opBoolean","INTERSECT",EDGE,{"derivedFrom":[makeQuery(id+"F15.opRevolve","SWEPT_FACE",FACE,{"disambiguationData":[OSD([sQuery(id+"F13.wireOp",EDGE,"E16.1")])]}),makeQuery(id+"F29.opRevolve","CAP_FACE",FACE,{"disambiguationData":[OSD([sQuery(id+"F28.wireOp",EDGE,"E40.bottom"),sQuery(id+"F28.wireOp",EDGE,"E40.top"),sQuery(id+"F28.wireOp",EDGE,"E40.left"),sQuery(id+"F28.wireOp",EDGE,"E40.right")])],"isStart":true})]});
            var Q14;
            {var subQ1=sQuery(id+"F28.wireOp",EDGE,"E40.left");Q14=makeQuery(id+"F29.boolean.opBoolean","COPY",EDGE,{"disambiguationData":[TD([makeQuery(id+"F15.opRevolve","SWEPT_FACE",FACE,{"disambiguationData":[OSD([sQuery(id+"F13.wireOp",EDGE,"E16.0")])]})])],"derivedFrom":makeQuery(id+"F29.opRevolve","CAP_EDGE",EDGE,{"disambiguationData":[OSD([subQ1])],"isStart":true})});}
            var Q15;
            {var subQ0=sQuery(id+"F28.wireOp",EDGE,"E40.right");var subQ1=sQuery(id+"F28.wireOp",EDGE,"E40.left");var subQ2=sQuery(id+"F28.wireOp",EDGE,"E40.top");var subQ3=sQuery(id+"F28.wireOp",EDGE,"E40.bottom");var subQ4=sQuery(id+"F13.wireOp",EDGE,"E16.2");Q15=makeQuery(id+"F37.boolean.opBoolean","MERGE",EDGE,{"derivedFrom":[makeQuery(id+"F29.boolean.opBoolean","COPY",EDGE,{"disambiguationData":[TD([makeQuery(id+"F14.opRevolve","SWEPT_FACE",FACE,{"disambiguationData":[OSD([sQuery(id+"F13.wireOp",EDGE,"E15.top")])]})])],"derivedFrom":makeQuery(id+"F29.opRevolve","CAP_EDGE",EDGE,{"disambiguationData":[OSD([subQ1])],"isStart":true})}),makeQuery(id+"F37.opExtrude","SWEPT_EDGE",EDGE,{"disambiguationData":[OSD([subQ4,subQ3,subQ2,subQ1,subQ0])]})]});}
            var Q16;
            Q16=makeQuery(id+"F29.boolean.opBoolean","INTERSECT",EDGE,{"derivedFrom":[makeQuery(id+"F15.opRevolve","SWEPT_FACE",FACE,{"disambiguationData":[OSD([sQuery(id+"F13.wireOp",EDGE,"E16.1")])]}),makeQuery(id+"F29.opRevolve","CAP_FACE",FACE,{"disambiguationData":[OSD([sQuery(id+"F28.wireOp",EDGE,"E40.bottom"),sQuery(id+"F28.wireOp",EDGE,"E40.top"),sQuery(id+"F28.wireOp",EDGE,"E40.left"),sQuery(id+"F28.wireOp",EDGE,"E40.right")])],"isStart":false})]});
            var Q17;
            {var subQ6=makeQuery(id+"F14.opRevolve","SWEPT_FACE",FACE,{"disambiguationData":[OSD([sQuery(id+"F13.wireOp",EDGE,"E16.1")])]});Q17=makeQuery(id+"F35.boolean.opBoolean","INTERSECT",EDGE,{"derivedFrom":[makeQuery(id+"F33.boolean.opBoolean","SPLIT",FACE,{"disambiguationData":[TD([makeQuery(id+"F19.boolean.opBoolean","COPY",FACE,{"derivedFrom":makeQuery(id+"F19.opExtrude","SWEPT_FACE",FACE,{"disambiguationData":[OSD([sQuery(id+"F18.wireOp",EDGE,"E26.bottom")])]})})])],"derivedFrom":subQ6}),makeQuery(id+"F35.opRevolve","CAP_FACE",FACE,{"disambiguationData":[OSD([sQuery(id+"F34.wireOp",EDGE,"E42.bottom"),sQuery(id+"F34.wireOp",EDGE,"E42.top"),sQuery(id+"F34.wireOp",EDGE,"E42.left"),sQuery(id+"F34.wireOp",EDGE,"E42.right")])],"isStart":false})]});}
            fillet(context, id + "F38", {"entities" : qUnion([Q0, Q1, Q2, Q3, Q4, Q5, Q6, Q7, Q8, Q9, Q10, Q11, Q12, Q13, Q14, Q15, Q16, Q17]), "radius" : 12 * mm, "tangentPropagation" : true, "allowEdgeOverflow" : false});
        }
        {
            var Q0;
            {var subQ0=sQuery(id+"F13.wireOp",EDGE,"E16.0");var subQ3=sQuery(id+"F13.wireOp",EDGE,"E16.1");var subQ5=sQuery(id+"F32.wireOp",EDGE,"E41.right");var subQ6=sQuery(id+"F32.wireOp",EDGE,"E41.left");var subQ7=sQuery(id+"F32.wireOp",EDGE,"E41.top");var subQ8=sQuery(id+"F32.wireOp",EDGE,"E41.bottom");var subQ9=makeQuery(id+"F33.opRevolve","CAP_FACE",FACE,{"disambiguationData":[OSD([subQ8,subQ7,subQ6,subQ5])],"isStart":false});Q0=makeQuery(id+"F35.boolean.opBoolean","SPLIT",EDGE,{"disambiguationData":[TD([makeQuery(id+"F35.opRevolve","CAP_FACE",FACE,{"disambiguationData":[OSD([sQuery(id+"F34.wireOp",EDGE,"E42.bottom"),sQuery(id+"F34.wireOp",EDGE,"E42.top"),sQuery(id+"F34.wireOp",EDGE,"E42.left"),sQuery(id+"F34.wireOp",EDGE,"E42.right")])],"isStart":true})])],"derivedFrom":makeQuery(id+"F33.boolean.opBoolean","SPLIT",EDGE,{"disambiguationData":[TD([subQ9])],"derivedFrom":makeQuery(id+"F15.opRevolve","SWEPT_EDGE",EDGE,{"disambiguationData":[OSD([subQ0,subQ3])]})})});}
            var Q1;
            Q1=makeQuery(id+"F35.boolean.opBoolean","INTERSECT",EDGE,{"derivedFrom":[makeQuery(id+"F15.opRevolve","SWEPT_FACE",FACE,{"disambiguationData":[OSD([sQuery(id+"F13.wireOp",EDGE,"E16.0")])]}),makeQuery(id+"F35.opRevolve","CAP_FACE",FACE,{"disambiguationData":[OSD([sQuery(id+"F34.wireOp",EDGE,"E42.bottom"),sQuery(id+"F34.wireOp",EDGE,"E42.top"),sQuery(id+"F34.wireOp",EDGE,"E42.left"),sQuery(id+"F34.wireOp",EDGE,"E42.right")])],"isStart":true})]});
            var Q2;
            Q2=makeQuery(id+"F35.boolean.opBoolean","INTERSECT",EDGE,{"derivedFrom":[makeQuery(id+"F15.opRevolve","SWEPT_FACE",FACE,{"disambiguationData":[OSD([sQuery(id+"F13.wireOp",EDGE,"E16.0")])]}),makeQuery(id+"F35.opRevolve","CAP_FACE",FACE,{"disambiguationData":[OSD([sQuery(id+"F34.wireOp",EDGE,"E42.bottom"),sQuery(id+"F34.wireOp",EDGE,"E42.top"),sQuery(id+"F34.wireOp",EDGE,"E42.left"),sQuery(id+"F34.wireOp",EDGE,"E42.right")])],"isStart":false})]});
            var Q3;
            {var subQ0=sQuery(id+"F13.wireOp",EDGE,"E16.0");var subQ2=sQuery(id+"F13.wireOp",EDGE,"E16.1");Q3=makeQuery(id+"F35.boolean.opBoolean","SPLIT",EDGE,{"disambiguationData":[TD([makeQuery(id+"F35.opRevolve","CAP_FACE",FACE,{"disambiguationData":[OSD([sQuery(id+"F34.wireOp",EDGE,"E42.bottom"),sQuery(id+"F34.wireOp",EDGE,"E42.top"),sQuery(id+"F34.wireOp",EDGE,"E42.left"),sQuery(id+"F34.wireOp",EDGE,"E42.right")])],"isStart":false})])],"derivedFrom":makeQuery(id+"F33.boolean.opBoolean","SPLIT",EDGE,{"disambiguationData":[TD([makeQuery(id+"F33.opRevolve","CAP_FACE",FACE,{"disambiguationData":[OSD([sQuery(id+"F32.wireOp",EDGE,"E41.bottom"),sQuery(id+"F32.wireOp",EDGE,"E41.top"),sQuery(id+"F32.wireOp",EDGE,"E41.left"),sQuery(id+"F32.wireOp",EDGE,"E41.right")])],"isStart":false})])],"derivedFrom":makeQuery(id+"F15.opRevolve","SWEPT_EDGE",EDGE,{"disambiguationData":[OSD([subQ0,subQ2])]})})});}
            var Q4;
            Q4=makeQuery(id+"F29.boolean.opBoolean","INTERSECT",EDGE,{"derivedFrom":[makeQuery(id+"F15.opRevolve","SWEPT_FACE",FACE,{"disambiguationData":[OSD([sQuery(id+"F13.wireOp",EDGE,"E16.0")])]}),makeQuery(id+"F29.opRevolve","CAP_FACE",FACE,{"disambiguationData":[OSD([sQuery(id+"F28.wireOp",EDGE,"E40.bottom"),sQuery(id+"F28.wireOp",EDGE,"E40.top"),sQuery(id+"F28.wireOp",EDGE,"E40.left"),sQuery(id+"F28.wireOp",EDGE,"E40.right")])],"isStart":true})]});
            var Q5;
            Q5=makeQuery(id+"F29.boolean.opBoolean","INTERSECT",EDGE,{"derivedFrom":[makeQuery(id+"F15.opRevolve","SWEPT_FACE",FACE,{"disambiguationData":[OSD([sQuery(id+"F13.wireOp",EDGE,"E16.0")])]}),makeQuery(id+"F29.opRevolve","CAP_FACE",FACE,{"disambiguationData":[OSD([sQuery(id+"F28.wireOp",EDGE,"E40.bottom"),sQuery(id+"F28.wireOp",EDGE,"E40.top"),sQuery(id+"F28.wireOp",EDGE,"E40.left"),sQuery(id+"F28.wireOp",EDGE,"E40.right")])],"isStart":false})]});
            var Q6;
            {var subQ0=sQuery(id+"F13.wireOp",EDGE,"E16.0");var subQ2=sQuery(id+"F13.wireOp",EDGE,"E16.1");Q6=makeQuery(id+"F33.boolean.opBoolean","SPLIT",EDGE,{"disambiguationData":[TD([makeQuery(id+"F33.opRevolve","CAP_FACE",FACE,{"disambiguationData":[OSD([sQuery(id+"F32.wireOp",EDGE,"E41.bottom"),sQuery(id+"F32.wireOp",EDGE,"E41.top"),sQuery(id+"F32.wireOp",EDGE,"E41.left"),sQuery(id+"F32.wireOp",EDGE,"E41.right")])],"isStart":true})])],"derivedFrom":makeQuery(id+"F15.opRevolve","SWEPT_EDGE",EDGE,{"disambiguationData":[OSD([subQ0,subQ2])]})});}
            var Q7;
            Q7=makeQuery(id+"F33.boolean.opBoolean","INTERSECT",EDGE,{"derivedFrom":[makeQuery(id+"F15.opRevolve","SWEPT_FACE",FACE,{"disambiguationData":[OSD([sQuery(id+"F13.wireOp",EDGE,"E16.0")])]}),makeQuery(id+"F33.opRevolve","CAP_FACE",FACE,{"disambiguationData":[OSD([sQuery(id+"F32.wireOp",EDGE,"E41.bottom"),sQuery(id+"F32.wireOp",EDGE,"E41.top"),sQuery(id+"F32.wireOp",EDGE,"E41.left"),sQuery(id+"F32.wireOp",EDGE,"E41.right")])],"isStart":true})]});
            var Q8;
            Q8=makeQuery(id+"F33.boolean.opBoolean","INTERSECT",EDGE,{"derivedFrom":[makeQuery(id+"F15.opRevolve","SWEPT_FACE",FACE,{"disambiguationData":[OSD([sQuery(id+"F13.wireOp",EDGE,"E16.0")])]}),makeQuery(id+"F33.opRevolve","CAP_FACE",FACE,{"disambiguationData":[OSD([sQuery(id+"F32.wireOp",EDGE,"E41.bottom"),sQuery(id+"F32.wireOp",EDGE,"E41.top"),sQuery(id+"F32.wireOp",EDGE,"E41.left"),sQuery(id+"F32.wireOp",EDGE,"E41.right")])],"isStart":false})]});
            var Q9;
            {var subQ0=sQuery(id+"F13.wireOp",EDGE,"E16.1");var subQ2=sQuery(id+"F13.wireOp",EDGE,"E16.2");var subQ10=sQuery(id+"F32.wireOp",EDGE,"E41.right");var subQ11=sQuery(id+"F32.wireOp",EDGE,"E41.left");var subQ12=sQuery(id+"F32.wireOp",EDGE,"E41.top");var subQ13=sQuery(id+"F32.wireOp",EDGE,"E41.bottom");var subQ14=makeQuery(id+"F33.opRevolve","CAP_FACE",FACE,{"disambiguationData":[OSD([subQ13,subQ12,subQ11,subQ10])],"isStart":false});Q9=makeQuery(id+"F35.boolean.opBoolean","SPLIT",EDGE,{"disambiguationData":[TD([makeQuery(id+"F35.opRevolve","CAP_FACE",FACE,{"disambiguationData":[OSD([sQuery(id+"F34.wireOp",EDGE,"E42.bottom"),sQuery(id+"F34.wireOp",EDGE,"E42.top"),sQuery(id+"F34.wireOp",EDGE,"E42.left"),sQuery(id+"F34.wireOp",EDGE,"E42.right")])],"isStart":true})])],"derivedFrom":makeQuery(id+"F33.boolean.opBoolean","SPLIT",EDGE,{"disambiguationData":[TD([subQ14])],"derivedFrom":makeQuery(id+"F14.opRevolve","SWEPT_EDGE",EDGE,{"disambiguationData":[OSD([subQ0,subQ2])]})})});}
            var Q10;
            Q10=makeQuery(id+"F35.boolean.opBoolean","INTERSECT",EDGE,{"derivedFrom":[makeQuery(id+"F14.opRevolve","SWEPT_FACE",FACE,{"disambiguationData":[OSD([sQuery(id+"F13.wireOp",EDGE,"E16.2")])]}),makeQuery(id+"F35.opRevolve","CAP_FACE",FACE,{"disambiguationData":[OSD([sQuery(id+"F34.wireOp",EDGE,"E42.bottom"),sQuery(id+"F34.wireOp",EDGE,"E42.top"),sQuery(id+"F34.wireOp",EDGE,"E42.left"),sQuery(id+"F34.wireOp",EDGE,"E42.right")])],"isStart":true})]});
            var Q11;
            Q11=makeQuery(id+"F35.boolean.opBoolean","INTERSECT",EDGE,{"derivedFrom":[makeQuery(id+"F14.opRevolve","SWEPT_FACE",FACE,{"disambiguationData":[OSD([sQuery(id+"F13.wireOp",EDGE,"E16.2")])]}),makeQuery(id+"F35.opRevolve","CAP_FACE",FACE,{"disambiguationData":[OSD([sQuery(id+"F34.wireOp",EDGE,"E42.bottom"),sQuery(id+"F34.wireOp",EDGE,"E42.top"),sQuery(id+"F34.wireOp",EDGE,"E42.left"),sQuery(id+"F34.wireOp",EDGE,"E42.right")])],"isStart":false})]});
            var Q12;
            {var subQ0=sQuery(id+"F13.wireOp",EDGE,"E16.1");var subQ2=sQuery(id+"F13.wireOp",EDGE,"E16.2");Q12=makeQuery(id+"F35.boolean.opBoolean","SPLIT",EDGE,{"disambiguationData":[TD([makeQuery(id+"F35.opRevolve","CAP_FACE",FACE,{"disambiguationData":[OSD([sQuery(id+"F34.wireOp",EDGE,"E42.bottom"),sQuery(id+"F34.wireOp",EDGE,"E42.top"),sQuery(id+"F34.wireOp",EDGE,"E42.left"),sQuery(id+"F34.wireOp",EDGE,"E42.right")])],"isStart":false})])],"derivedFrom":makeQuery(id+"F33.boolean.opBoolean","SPLIT",EDGE,{"disambiguationData":[TD([makeQuery(id+"F33.opRevolve","CAP_FACE",FACE,{"disambiguationData":[OSD([sQuery(id+"F32.wireOp",EDGE,"E41.bottom"),sQuery(id+"F32.wireOp",EDGE,"E41.top"),sQuery(id+"F32.wireOp",EDGE,"E41.left"),sQuery(id+"F32.wireOp",EDGE,"E41.right")])],"isStart":false})])],"derivedFrom":makeQuery(id+"F14.opRevolve","SWEPT_EDGE",EDGE,{"disambiguationData":[OSD([subQ0,subQ2])]})})});}
            var Q13;
            Q13=makeQuery(id+"F29.boolean.opBoolean","INTERSECT",EDGE,{"derivedFrom":[makeQuery(id+"F14.opRevolve","SWEPT_FACE",FACE,{"disambiguationData":[OSD([sQuery(id+"F13.wireOp",EDGE,"E16.2")])]}),makeQuery(id+"F29.opRevolve","CAP_FACE",FACE,{"disambiguationData":[OSD([sQuery(id+"F28.wireOp",EDGE,"E40.bottom"),sQuery(id+"F28.wireOp",EDGE,"E40.top"),sQuery(id+"F28.wireOp",EDGE,"E40.left"),sQuery(id+"F28.wireOp",EDGE,"E40.right")])],"isStart":true})]});
            var Q14;
            Q14=makeQuery(id+"F29.boolean.opBoolean","INTERSECT",EDGE,{"derivedFrom":[makeQuery(id+"F14.opRevolve","SWEPT_FACE",FACE,{"disambiguationData":[OSD([sQuery(id+"F13.wireOp",EDGE,"E16.2")])]}),makeQuery(id+"F29.opRevolve","CAP_FACE",FACE,{"disambiguationData":[OSD([sQuery(id+"F28.wireOp",EDGE,"E40.bottom"),sQuery(id+"F28.wireOp",EDGE,"E40.top"),sQuery(id+"F28.wireOp",EDGE,"E40.left"),sQuery(id+"F28.wireOp",EDGE,"E40.right")])],"isStart":false})]});
            var Q15;
            {var subQ0=sQuery(id+"F13.wireOp",EDGE,"E16.1");var subQ2=sQuery(id+"F13.wireOp",EDGE,"E16.2");Q15=makeQuery(id+"F33.boolean.opBoolean","SPLIT",EDGE,{"disambiguationData":[TD([makeQuery(id+"F33.opRevolve","CAP_FACE",FACE,{"disambiguationData":[OSD([sQuery(id+"F32.wireOp",EDGE,"E41.bottom"),sQuery(id+"F32.wireOp",EDGE,"E41.top"),sQuery(id+"F32.wireOp",EDGE,"E41.left"),sQuery(id+"F32.wireOp",EDGE,"E41.right")])],"isStart":true})])],"derivedFrom":makeQuery(id+"F14.opRevolve","SWEPT_EDGE",EDGE,{"disambiguationData":[OSD([subQ0,subQ2])]})});}
            var Q16;
            Q16=makeQuery(id+"F33.boolean.opBoolean","INTERSECT",EDGE,{"derivedFrom":[makeQuery(id+"F14.opRevolve","SWEPT_FACE",FACE,{"disambiguationData":[OSD([sQuery(id+"F13.wireOp",EDGE,"E16.2")])]}),makeQuery(id+"F33.opRevolve","CAP_FACE",FACE,{"disambiguationData":[OSD([sQuery(id+"F32.wireOp",EDGE,"E41.bottom"),sQuery(id+"F32.wireOp",EDGE,"E41.top"),sQuery(id+"F32.wireOp",EDGE,"E41.left"),sQuery(id+"F32.wireOp",EDGE,"E41.right")])],"isStart":true})]});
            var Q17;
            Q17=makeQuery(id+"F33.boolean.opBoolean","INTERSECT",EDGE,{"derivedFrom":[makeQuery(id+"F14.opRevolve","SWEPT_FACE",FACE,{"disambiguationData":[OSD([sQuery(id+"F13.wireOp",EDGE,"E16.2")])]}),makeQuery(id+"F33.opRevolve","CAP_FACE",FACE,{"disambiguationData":[OSD([sQuery(id+"F32.wireOp",EDGE,"E41.bottom"),sQuery(id+"F32.wireOp",EDGE,"E41.top"),sQuery(id+"F32.wireOp",EDGE,"E41.left"),sQuery(id+"F32.wireOp",EDGE,"E41.right")])],"isStart":false})]});
            var Q18;
            {var subQ0=makeQuery(id+"F15.opRevolve","SWEPT_FACE",FACE,{"disambiguationData":[OSD([sQuery(id+"F13.wireOp",EDGE,"E16.0")])]});var subQ1=sQuery(id+"F32.wireOp",EDGE,"E41.right");Q18=makeQuery(id+"F38.opFillet","BLEND_EDGE",EDGE,{"blendedFrom":[makeQuery(id+"F33.boolean.opBoolean","COPY",EDGE,{"disambiguationData":[TD([subQ0])],"derivedFrom":makeQuery(id+"F33.opRevolve","CAP_EDGE",EDGE,{"disambiguationData":[OSD([subQ1])],"isStart":true})}),subQ0],"blendedInto":[subQ0]});}
            var Q19;
            Q19=makeQuery(id+"F38.opFillet","BLEND_EDGE",EDGE,{"blendedFrom":[makeQuery(id+"F33.boolean.opBoolean","INTERSECT",EDGE,{"derivedFrom":[makeQuery(id+"F15.opRevolve","SWEPT_FACE",FACE,{"disambiguationData":[OSD([sQuery(id+"F13.wireOp",EDGE,"E16.1")])]}),makeQuery(id+"F33.opRevolve","CAP_FACE",FACE,{"disambiguationData":[OSD([sQuery(id+"F32.wireOp",EDGE,"E41.bottom"),sQuery(id+"F32.wireOp",EDGE,"E41.top"),sQuery(id+"F32.wireOp",EDGE,"E41.left"),sQuery(id+"F32.wireOp",EDGE,"E41.right")])],"isStart":true})]}),makeQuery(id+"F15.opRevolve","SWEPT_FACE",FACE,{"disambiguationData":[OSD([sQuery(id+"F13.wireOp",EDGE,"E16.0")])]})],"blendedInto":[makeQuery(id+"F15.opRevolve","SWEPT_FACE",FACE,{"disambiguationData":[OSD([sQuery(id+"F13.wireOp",EDGE,"E16.0")])]})]});
            var Q20;
            Q20=makeQuery(id+"F38.opFillet","BLEND_EDGE",EDGE,{"blendedFrom":[makeQuery(id+"F29.boolean.opBoolean","INTERSECT",EDGE,{"derivedFrom":[makeQuery(id+"F15.opRevolve","SWEPT_FACE",FACE,{"disambiguationData":[OSD([sQuery(id+"F13.wireOp",EDGE,"E16.1")])]}),makeQuery(id+"F29.opRevolve","CAP_FACE",FACE,{"disambiguationData":[OSD([sQuery(id+"F28.wireOp",EDGE,"E40.bottom"),sQuery(id+"F28.wireOp",EDGE,"E40.top"),sQuery(id+"F28.wireOp",EDGE,"E40.left"),sQuery(id+"F28.wireOp",EDGE,"E40.right")])],"isStart":false})]}),makeQuery(id+"F15.opRevolve","SWEPT_FACE",FACE,{"disambiguationData":[OSD([sQuery(id+"F13.wireOp",EDGE,"E16.0")])]})],"blendedInto":[makeQuery(id+"F15.opRevolve","SWEPT_FACE",FACE,{"disambiguationData":[OSD([sQuery(id+"F13.wireOp",EDGE,"E16.0")])]})]});
            var Q21;
            {var subQ0=makeQuery(id+"F15.opRevolve","SWEPT_FACE",FACE,{"disambiguationData":[OSD([sQuery(id+"F13.wireOp",EDGE,"E16.0")])]});var subQ2=sQuery(id+"F28.wireOp",EDGE,"E40.left");Q21=makeQuery(id+"F38.opFillet","BLEND_EDGE",EDGE,{"blendedFrom":[makeQuery(id+"F29.boolean.opBoolean","COPY",EDGE,{"disambiguationData":[TD([subQ0])],"derivedFrom":makeQuery(id+"F29.opRevolve","CAP_EDGE",EDGE,{"disambiguationData":[OSD([subQ2])],"isStart":true})}),subQ0],"blendedInto":[subQ0]});}
            var Q22;
            Q22=makeQuery(id+"F38.opFillet","BLEND_EDGE",EDGE,{"blendedFrom":[makeQuery(id+"F29.boolean.opBoolean","INTERSECT",EDGE,{"derivedFrom":[makeQuery(id+"F15.opRevolve","SWEPT_FACE",FACE,{"disambiguationData":[OSD([sQuery(id+"F13.wireOp",EDGE,"E16.1")])]}),makeQuery(id+"F29.opRevolve","CAP_FACE",FACE,{"disambiguationData":[OSD([sQuery(id+"F28.wireOp",EDGE,"E40.bottom"),sQuery(id+"F28.wireOp",EDGE,"E40.top"),sQuery(id+"F28.wireOp",EDGE,"E40.left"),sQuery(id+"F28.wireOp",EDGE,"E40.right")])],"isStart":true})]}),makeQuery(id+"F15.opRevolve","SWEPT_FACE",FACE,{"disambiguationData":[OSD([sQuery(id+"F13.wireOp",EDGE,"E16.0")])]})],"blendedInto":[makeQuery(id+"F15.opRevolve","SWEPT_FACE",FACE,{"disambiguationData":[OSD([sQuery(id+"F13.wireOp",EDGE,"E16.0")])]})]});
            var Q23;
            {var subQ0=makeQuery(id+"F15.opRevolve","SWEPT_FACE",FACE,{"disambiguationData":[OSD([sQuery(id+"F13.wireOp",EDGE,"E16.0")])]});var subQ2=makeQuery(id+"F15.opRevolve","SWEPT_FACE",FACE,{"disambiguationData":[OSD([sQuery(id+"F13.wireOp",EDGE,"E16.1")])]});Q23=makeQuery(id+"F38.opFillet","BLEND_EDGE",EDGE,{"blendedFrom":[makeQuery(id+"F35.boolean.opBoolean","INTERSECT",EDGE,{"derivedFrom":[makeQuery(id+"F33.boolean.opBoolean","SPLIT",FACE,{"disambiguationData":[TD([makeQuery(id+"F33.opRevolve","CAP_FACE",FACE,{"disambiguationData":[OSD([sQuery(id+"F32.wireOp",EDGE,"E41.bottom"),sQuery(id+"F32.wireOp",EDGE,"E41.top"),sQuery(id+"F32.wireOp",EDGE,"E41.left"),sQuery(id+"F32.wireOp",EDGE,"E41.right")])],"isStart":false})])],"derivedFrom":subQ2}),makeQuery(id+"F35.opRevolve","CAP_FACE",FACE,{"disambiguationData":[OSD([sQuery(id+"F34.wireOp",EDGE,"E42.bottom"),sQuery(id+"F34.wireOp",EDGE,"E42.top"),sQuery(id+"F34.wireOp",EDGE,"E42.left"),sQuery(id+"F34.wireOp",EDGE,"E42.right")])],"isStart":false})]}),subQ0],"blendedInto":[subQ0]});}
            var Q24;
            {var subQ0=makeQuery(id+"F15.opRevolve","SWEPT_FACE",FACE,{"disambiguationData":[OSD([sQuery(id+"F13.wireOp",EDGE,"E16.0")])]});var subQ1=sQuery(id+"F34.wireOp",EDGE,"E42.right");Q24=makeQuery(id+"F38.opFillet","BLEND_EDGE",EDGE,{"blendedFrom":[makeQuery(id+"F35.boolean.opBoolean","COPY",EDGE,{"disambiguationData":[TD([subQ0])],"derivedFrom":makeQuery(id+"F35.opRevolve","CAP_EDGE",EDGE,{"disambiguationData":[OSD([subQ1])],"isStart":true})}),subQ0],"blendedInto":[subQ0]});}
            var Q25;
            {var subQ0=makeQuery(id+"F15.opRevolve","SWEPT_FACE",FACE,{"disambiguationData":[OSD([sQuery(id+"F13.wireOp",EDGE,"E16.0")])]});var subQ2=makeQuery(id+"F15.opRevolve","SWEPT_FACE",FACE,{"disambiguationData":[OSD([sQuery(id+"F13.wireOp",EDGE,"E16.1")])]});Q25=makeQuery(id+"F38.opFillet","BLEND_EDGE",EDGE,{"blendedFrom":[makeQuery(id+"F35.boolean.opBoolean","INTERSECT",EDGE,{"derivedFrom":[makeQuery(id+"F33.boolean.opBoolean","SPLIT",FACE,{"disambiguationData":[TD([makeQuery(id+"F33.opRevolve","CAP_FACE",FACE,{"disambiguationData":[OSD([sQuery(id+"F32.wireOp",EDGE,"E41.bottom"),sQuery(id+"F32.wireOp",EDGE,"E41.top"),sQuery(id+"F32.wireOp",EDGE,"E41.left"),sQuery(id+"F32.wireOp",EDGE,"E41.right")])],"isStart":false})])],"derivedFrom":subQ2}),makeQuery(id+"F35.opRevolve","CAP_FACE",FACE,{"disambiguationData":[OSD([sQuery(id+"F34.wireOp",EDGE,"E42.bottom"),sQuery(id+"F34.wireOp",EDGE,"E42.top"),sQuery(id+"F34.wireOp",EDGE,"E42.left"),sQuery(id+"F34.wireOp",EDGE,"E42.right")])],"isStart":true})]}),subQ0],"blendedInto":[subQ0]});}
            var Q26;
            Q26=makeQuery(id+"F38.opFillet","BLEND_EDGE",EDGE,{"blendedFrom":[makeQuery(id+"F33.boolean.opBoolean","INTERSECT",EDGE,{"derivedFrom":[makeQuery(id+"F15.opRevolve","SWEPT_FACE",FACE,{"disambiguationData":[OSD([sQuery(id+"F13.wireOp",EDGE,"E16.1")])]}),makeQuery(id+"F33.opRevolve","CAP_FACE",FACE,{"disambiguationData":[OSD([sQuery(id+"F32.wireOp",EDGE,"E41.bottom"),sQuery(id+"F32.wireOp",EDGE,"E41.top"),sQuery(id+"F32.wireOp",EDGE,"E41.left"),sQuery(id+"F32.wireOp",EDGE,"E41.right")])],"isStart":false})]}),makeQuery(id+"F15.opRevolve","SWEPT_FACE",FACE,{"disambiguationData":[OSD([sQuery(id+"F13.wireOp",EDGE,"E16.0")])]})],"blendedInto":[makeQuery(id+"F15.opRevolve","SWEPT_FACE",FACE,{"disambiguationData":[OSD([sQuery(id+"F13.wireOp",EDGE,"E16.0")])]})]});
            var Q27;
            Q27=makeQuery(id+"F38.opFillet","BLEND_EDGE",EDGE,{"blendedFrom":[makeQuery(id+"F29.boolean.opBoolean","INTERSECT",EDGE,{"derivedFrom":[makeQuery(id+"F14.opRevolve","SWEPT_FACE",FACE,{"disambiguationData":[OSD([sQuery(id+"F13.wireOp",EDGE,"E16.1")])]}),makeQuery(id+"F29.opRevolve","CAP_FACE",FACE,{"disambiguationData":[OSD([sQuery(id+"F28.wireOp",EDGE,"E40.bottom"),sQuery(id+"F28.wireOp",EDGE,"E40.top"),sQuery(id+"F28.wireOp",EDGE,"E40.left"),sQuery(id+"F28.wireOp",EDGE,"E40.right")])],"isStart":false})]}),makeQuery(id+"F14.opRevolve","SWEPT_FACE",FACE,{"disambiguationData":[OSD([sQuery(id+"F13.wireOp",EDGE,"E16.2")])]})],"blendedInto":[makeQuery(id+"F14.opRevolve","SWEPT_FACE",FACE,{"disambiguationData":[OSD([sQuery(id+"F13.wireOp",EDGE,"E16.2")])]})]});
            var Q28;
            Q28=makeQuery(id+"F38.opFillet","BLEND_EDGE",EDGE,{"blendedFrom":[makeQuery(id+"F33.boolean.opBoolean","INTERSECT",EDGE,{"derivedFrom":[makeQuery(id+"F14.opRevolve","SWEPT_FACE",FACE,{"disambiguationData":[OSD([sQuery(id+"F13.wireOp",EDGE,"E16.1")])]}),makeQuery(id+"F33.opRevolve","CAP_FACE",FACE,{"disambiguationData":[OSD([sQuery(id+"F32.wireOp",EDGE,"E41.bottom"),sQuery(id+"F32.wireOp",EDGE,"E41.top"),sQuery(id+"F32.wireOp",EDGE,"E41.left"),sQuery(id+"F32.wireOp",EDGE,"E41.right")])],"isStart":true})]}),makeQuery(id+"F14.opRevolve","SWEPT_FACE",FACE,{"disambiguationData":[OSD([sQuery(id+"F13.wireOp",EDGE,"E16.2")])]})],"blendedInto":[makeQuery(id+"F14.opRevolve","SWEPT_FACE",FACE,{"disambiguationData":[OSD([sQuery(id+"F13.wireOp",EDGE,"E16.2")])]})]});
            var Q29;
            {var subQ0=sQuery(id+"F13.wireOp",EDGE,"E16.2");var subQ1=makeQuery(id+"F14.opRevolve","SWEPT_FACE",FACE,{"disambiguationData":[OSD([subQ0])]});var subQ2=sQuery(id+"F32.wireOp",EDGE,"E41.right");var subQ3=sQuery(id+"F32.wireOp",EDGE,"E41.left");var subQ4=sQuery(id+"F32.wireOp",EDGE,"E41.top");var subQ5=sQuery(id+"F32.wireOp",EDGE,"E41.bottom");Q29=makeQuery(id+"F38.opFillet","BLEND_EDGE",EDGE,{"blendedFrom":[makeQuery(id+"F37.boolean.opBoolean","MERGE",EDGE,{"derivedFrom":[makeQuery(id+"F33.boolean.opBoolean","COPY",EDGE,{"disambiguationData":[TD([makeQuery(id+"F14.opRevolve","SWEPT_FACE",FACE,{"disambiguationData":[OSD([sQuery(id+"F13.wireOp",EDGE,"E15.top")])]})])],"derivedFrom":makeQuery(id+"F33.opRevolve","CAP_EDGE",EDGE,{"disambiguationData":[OSD([subQ2])],"isStart":true})}),makeQuery(id+"F37.opExtrude","SWEPT_EDGE",EDGE,{"disambiguationData":[OSD([subQ0,subQ5,subQ4,subQ3,subQ2])]})]}),subQ1],"blendedInto":[subQ1]});}
            var Q30;
            Q30=makeQuery(id+"F38.opFillet","BLEND_EDGE",EDGE,{"blendedFrom":[makeQuery(id+"F33.boolean.opBoolean","INTERSECT",EDGE,{"derivedFrom":[makeQuery(id+"F14.opRevolve","SWEPT_FACE",FACE,{"disambiguationData":[OSD([sQuery(id+"F13.wireOp",EDGE,"E16.1")])]}),makeQuery(id+"F33.opRevolve","CAP_FACE",FACE,{"disambiguationData":[OSD([sQuery(id+"F32.wireOp",EDGE,"E41.bottom"),sQuery(id+"F32.wireOp",EDGE,"E41.top"),sQuery(id+"F32.wireOp",EDGE,"E41.left"),sQuery(id+"F32.wireOp",EDGE,"E41.right")])],"isStart":false})]}),makeQuery(id+"F14.opRevolve","SWEPT_FACE",FACE,{"disambiguationData":[OSD([sQuery(id+"F13.wireOp",EDGE,"E16.2")])]})],"blendedInto":[makeQuery(id+"F14.opRevolve","SWEPT_FACE",FACE,{"disambiguationData":[OSD([sQuery(id+"F13.wireOp",EDGE,"E16.2")])]})]});
            var Q31;
            {var subQ0=makeQuery(id+"F14.opRevolve","SWEPT_FACE",FACE,{"disambiguationData":[OSD([sQuery(id+"F13.wireOp",EDGE,"E16.2")])]});var subQ6=makeQuery(id+"F14.opRevolve","SWEPT_FACE",FACE,{"disambiguationData":[OSD([sQuery(id+"F13.wireOp",EDGE,"E16.1")])]});Q31=makeQuery(id+"F38.opFillet","BLEND_EDGE",EDGE,{"blendedFrom":[makeQuery(id+"F35.boolean.opBoolean","INTERSECT",EDGE,{"derivedFrom":[makeQuery(id+"F33.boolean.opBoolean","SPLIT",FACE,{"disambiguationData":[TD([makeQuery(id+"F19.boolean.opBoolean","COPY",FACE,{"derivedFrom":makeQuery(id+"F19.opExtrude","SWEPT_FACE",FACE,{"disambiguationData":[OSD([sQuery(id+"F18.wireOp",EDGE,"E26.bottom")])]})})])],"derivedFrom":subQ6}),makeQuery(id+"F35.opRevolve","CAP_FACE",FACE,{"disambiguationData":[OSD([sQuery(id+"F34.wireOp",EDGE,"E42.bottom"),sQuery(id+"F34.wireOp",EDGE,"E42.top"),sQuery(id+"F34.wireOp",EDGE,"E42.left"),sQuery(id+"F34.wireOp",EDGE,"E42.right")])],"isStart":true})]}),subQ0],"blendedInto":[subQ0]});}
            var Q32;
            {var subQ0=sQuery(id+"F13.wireOp",EDGE,"E16.2");var subQ1=makeQuery(id+"F14.opRevolve","SWEPT_FACE",FACE,{"disambiguationData":[OSD([subQ0])]});var subQ2=sQuery(id+"F34.wireOp",EDGE,"E42.right");var subQ3=sQuery(id+"F34.wireOp",EDGE,"E42.left");var subQ4=sQuery(id+"F34.wireOp",EDGE,"E42.top");var subQ5=sQuery(id+"F34.wireOp",EDGE,"E42.bottom");Q32=makeQuery(id+"F38.opFillet","BLEND_EDGE",EDGE,{"blendedFrom":[makeQuery(id+"F37.boolean.opBoolean","MERGE",EDGE,{"derivedFrom":[makeQuery(id+"F35.boolean.opBoolean","COPY",EDGE,{"disambiguationData":[TD([makeQuery(id+"F14.opRevolve","SWEPT_FACE",FACE,{"disambiguationData":[OSD([sQuery(id+"F13.wireOp",EDGE,"E15.top")])]})])],"derivedFrom":makeQuery(id+"F35.opRevolve","CAP_EDGE",EDGE,{"disambiguationData":[OSD([subQ2])],"isStart":true})}),makeQuery(id+"F37.opExtrude","SWEPT_EDGE",EDGE,{"disambiguationData":[OSD([subQ0,subQ5,subQ4,subQ3,subQ2])]})]}),subQ1],"blendedInto":[subQ1]});}
            var Q33;
            {var subQ0=makeQuery(id+"F14.opRevolve","SWEPT_FACE",FACE,{"disambiguationData":[OSD([sQuery(id+"F13.wireOp",EDGE,"E16.2")])]});var subQ6=makeQuery(id+"F14.opRevolve","SWEPT_FACE",FACE,{"disambiguationData":[OSD([sQuery(id+"F13.wireOp",EDGE,"E16.1")])]});Q33=makeQuery(id+"F38.opFillet","BLEND_EDGE",EDGE,{"blendedFrom":[makeQuery(id+"F35.boolean.opBoolean","INTERSECT",EDGE,{"derivedFrom":[makeQuery(id+"F33.boolean.opBoolean","SPLIT",FACE,{"disambiguationData":[TD([makeQuery(id+"F19.boolean.opBoolean","COPY",FACE,{"derivedFrom":makeQuery(id+"F19.opExtrude","SWEPT_FACE",FACE,{"disambiguationData":[OSD([sQuery(id+"F18.wireOp",EDGE,"E26.bottom")])]})})])],"derivedFrom":subQ6}),makeQuery(id+"F35.opRevolve","CAP_FACE",FACE,{"disambiguationData":[OSD([sQuery(id+"F34.wireOp",EDGE,"E42.bottom"),sQuery(id+"F34.wireOp",EDGE,"E42.top"),sQuery(id+"F34.wireOp",EDGE,"E42.left"),sQuery(id+"F34.wireOp",EDGE,"E42.right")])],"isStart":false})]}),subQ0],"blendedInto":[subQ0]});}
            var Q34;
            Q34=makeQuery(id+"F38.opFillet","BLEND_EDGE",EDGE,{"blendedFrom":[makeQuery(id+"F29.boolean.opBoolean","INTERSECT",EDGE,{"derivedFrom":[makeQuery(id+"F14.opRevolve","SWEPT_FACE",FACE,{"disambiguationData":[OSD([sQuery(id+"F13.wireOp",EDGE,"E16.1")])]}),makeQuery(id+"F29.opRevolve","CAP_FACE",FACE,{"disambiguationData":[OSD([sQuery(id+"F28.wireOp",EDGE,"E40.bottom"),sQuery(id+"F28.wireOp",EDGE,"E40.top"),sQuery(id+"F28.wireOp",EDGE,"E40.left"),sQuery(id+"F28.wireOp",EDGE,"E40.right")])],"isStart":true})]}),makeQuery(id+"F14.opRevolve","SWEPT_FACE",FACE,{"disambiguationData":[OSD([sQuery(id+"F13.wireOp",EDGE,"E16.2")])]})],"blendedInto":[makeQuery(id+"F14.opRevolve","SWEPT_FACE",FACE,{"disambiguationData":[OSD([sQuery(id+"F13.wireOp",EDGE,"E16.2")])]})]});
            var Q35;
            {var subQ0=sQuery(id+"F13.wireOp",EDGE,"E16.2");var subQ1=makeQuery(id+"F14.opRevolve","SWEPT_FACE",FACE,{"disambiguationData":[OSD([subQ0])]});var subQ2=sQuery(id+"F28.wireOp",EDGE,"E40.right");var subQ3=sQuery(id+"F28.wireOp",EDGE,"E40.left");var subQ4=sQuery(id+"F28.wireOp",EDGE,"E40.top");var subQ5=sQuery(id+"F28.wireOp",EDGE,"E40.bottom");Q35=makeQuery(id+"F38.opFillet","BLEND_EDGE",EDGE,{"blendedFrom":[makeQuery(id+"F37.boolean.opBoolean","MERGE",EDGE,{"derivedFrom":[makeQuery(id+"F29.boolean.opBoolean","COPY",EDGE,{"disambiguationData":[TD([makeQuery(id+"F14.opRevolve","SWEPT_FACE",FACE,{"disambiguationData":[OSD([sQuery(id+"F13.wireOp",EDGE,"E15.top")])]})])],"derivedFrom":makeQuery(id+"F29.opRevolve","CAP_EDGE",EDGE,{"disambiguationData":[OSD([subQ3])],"isStart":true})}),makeQuery(id+"F37.opExtrude","SWEPT_EDGE",EDGE,{"disambiguationData":[OSD([subQ0,subQ5,subQ4,subQ3,subQ2])]})]}),subQ1],"blendedInto":[subQ1]});}
            fillet(context, id + "F39", {"entities" : qUnion([Q0, Q1, Q2, Q3, Q4, Q5, Q6, Q7, Q8, Q9, Q10, Q11, Q12, Q13, Q14, Q15, Q16, Q17, Q18, Q19, Q20, Q21, Q22, Q23, Q24, Q25, Q26, Q27, Q28, Q29, Q30, Q31, Q32, Q33, Q34, Q35]), "radius" : 4 * mm, "tangentPropagation" : true, "allowEdgeOverflow" : false});
        }
        {
            var Q0;
            {var subQ0=sQuery(id+"F32.wireOp",EDGE,"E41.right");var subQ1=sQuery(id+"F32.wireOp",EDGE,"E41.left");var subQ2=sQuery(id+"F32.wireOp",EDGE,"E41.top");var subQ3=sQuery(id+"F32.wireOp",EDGE,"E41.bottom");var subQ4=makeQuery(id+"F33.opRevolve","CAP_FACE",FACE,{"disambiguationData":[OSD([subQ3,subQ2,subQ1,subQ0])],"isStart":true});var subQ5=sQuery(id+"F13.wireOp",EDGE,"E16.2");var subQ6=makeQuery(id+"F14.opRevolve","SWEPT_FACE",FACE,{"disambiguationData":[OSD([subQ5])]});Q0=makeQuery(id+"F37.boolean.opBoolean","MERGE",FACE,{"derivedFrom":[makeQuery(id+"F33.boolean.opBoolean","COPY",FACE,{"disambiguationData":[TD([makeQuery(id+"F14.opRevolve","SWEPT_FACE",FACE,{"disambiguationData":[OSD([sQuery(id+"F13.wireOp",EDGE,"E15.top")])]})])],"derivedFrom":subQ4}),makeQuery(id+"F37.opExtrude","SWEPT_FACE",FACE,{"disambiguationData":[OSD([subQ5,subQ3,subQ2,subQ1,subQ0]),TDD([makeQuery(id+"F36.imprint","IMPRINT",EDGE,{"derivedFrom":makeQuery(id+"F33.boolean.opBoolean","INTERSECT",EDGE,{"derivedFrom":[subQ6,subQ4]})})])]})]});}
            var sketch = newSketch(context, id + "F40", { "sketchPlane" : qUnion([Q0])});
            skCircle(sketch, "E50", {"center": v(-26.07, 0) * mm, "radius": 6 * mm});
            skSolve(sketch);
        }
        {
            var Q0;
            {var subQ0=sQuery(id+"F34.wireOp",EDGE,"E42.right");var subQ1=sQuery(id+"F34.wireOp",EDGE,"E42.left");var subQ2=sQuery(id+"F34.wireOp",EDGE,"E42.top");var subQ3=sQuery(id+"F34.wireOp",EDGE,"E42.bottom");var subQ4=makeQuery(id+"F35.opRevolve","CAP_FACE",FACE,{"disambiguationData":[OSD([subQ3,subQ2,subQ1,subQ0])],"isStart":true});var subQ5=sQuery(id+"F13.wireOp",EDGE,"E16.2");var subQ6=makeQuery(id+"F14.opRevolve","SWEPT_FACE",FACE,{"disambiguationData":[OSD([subQ5])]});Q0=makeQuery(id+"F37.boolean.opBoolean","MERGE",FACE,{"derivedFrom":[makeQuery(id+"F35.boolean.opBoolean","COPY",FACE,{"disambiguationData":[TD([makeQuery(id+"F14.opRevolve","SWEPT_FACE",FACE,{"disambiguationData":[OSD([sQuery(id+"F13.wireOp",EDGE,"E15.top")])]})])],"derivedFrom":subQ4}),makeQuery(id+"F37.opExtrude","SWEPT_FACE",FACE,{"disambiguationData":[OSD([subQ5,subQ3,subQ2,subQ1,subQ0]),TDD([makeQuery(id+"F36.imprint","IMPRINT",EDGE,{"derivedFrom":makeQuery(id+"F35.boolean.opBoolean","INTERSECT",EDGE,{"derivedFrom":[subQ6,subQ4]})})])]})]});}
            var sketch = newSketch(context, id + "F41", { "sketchPlane" : qUnion([Q0])});
            skCircle(sketch, "E51", {"center": v(-26.07, 0) * mm, "radius": 6 * mm});
            skSolve(sketch);
        }
        {
            var Q0;
            {var subQ0=sQuery(id+"F28.wireOp",EDGE,"E40.right");var subQ1=sQuery(id+"F28.wireOp",EDGE,"E40.left");var subQ2=sQuery(id+"F28.wireOp",EDGE,"E40.top");var subQ3=sQuery(id+"F28.wireOp",EDGE,"E40.bottom");var subQ4=makeQuery(id+"F29.opRevolve","CAP_FACE",FACE,{"disambiguationData":[OSD([subQ3,subQ2,subQ1,subQ0])],"isStart":true});var subQ5=sQuery(id+"F13.wireOp",EDGE,"E16.2");var subQ6=makeQuery(id+"F14.opRevolve","SWEPT_FACE",FACE,{"disambiguationData":[OSD([subQ5])]});Q0=makeQuery(id+"F37.boolean.opBoolean","MERGE",FACE,{"derivedFrom":[makeQuery(id+"F29.boolean.opBoolean","COPY",FACE,{"disambiguationData":[TD([makeQuery(id+"F14.opRevolve","SWEPT_FACE",FACE,{"disambiguationData":[OSD([sQuery(id+"F13.wireOp",EDGE,"E15.top")])]})])],"derivedFrom":subQ4}),makeQuery(id+"F37.opExtrude","SWEPT_FACE",FACE,{"disambiguationData":[OSD([subQ5,subQ3,subQ2,subQ1,subQ0]),TDD([makeQuery(id+"F36.imprint","IMPRINT",EDGE,{"derivedFrom":makeQuery(id+"F29.boolean.opBoolean","INTERSECT",EDGE,{"derivedFrom":[subQ6,subQ4]})})])]})]});}
            var sketch = newSketch(context, id + "F42", { "sketchPlane" : qUnion([Q0])});
            skCircle(sketch, "E52", {"center": v(-31.02, 2) * mm, "radius": 6 * mm});
            skSolve(sketch);
        }
        {
            var Q0;
            Q0 = qSketchRegion(id + "F40", true);
            extrude(context, id + "F43", {"entities" : qUnion([Q0]), "operationType" : NewBodyOperationType.REMOVE, "oppositeDirection" : true, "depth" : 26 * mm, "offsetDistance" : 25 * mm});
        }
        {
            var Q0;
            Q0 = qSketchRegion(id + "F41", true);
            extrude(context, id + "F44", {"entities" : qUnion([Q0]), "operationType" : NewBodyOperationType.REMOVE, "oppositeDirection" : true, "depth" : 25 * mm, "offsetDistance" : 25 * mm});
        }
        {
            var Q0;
            Q0 = qSketchRegion(id + "F42", true);
            extrude(context, id + "F45", {"entities" : qUnion([Q0]), "operationType" : NewBodyOperationType.REMOVE, "oppositeDirection" : true, "depth" : 25 * mm, "offsetDistance" : 25 * mm});
        }
        {
            var Q0;
            Q0=makeQuery(id+"F15.opRevolve","SWEPT_FACE",FACE,{"disambiguationData":[OSD([sQuery(id+"F13.wireOp",EDGE,"E16.0")])]});
            var sketch = newSketch(context, id + "F46", { "sketchPlane" : qUnion([Q0])});
            skCircle(sketch, "E53", {"center": v(0, -38) * mm, "radius": 1.69 * mm});
            skCircle(sketch, "E54.1.0", {"center": v(31.76, 17.01) * mm, "radius": 1.69 * mm});
            skCircle(sketch, "E54.2.0", {"center": v(-31.76, 17.01) * mm, "radius": 1.69 * mm});
            skCircle(sketch, "E55", {"center": v(28, 60) * mm, "radius": 1.5 * mm});
            skCircle(sketch, "E56.1.0", {"center": v(-36.31, -54.45) * mm, "radius": 1.5 * mm});
            skCircle(sketch, "E56.2.0", {"center": v(65.31, -4.22) * mm, "radius": 1.5 * mm});
            skPoint(sketch, "E56.center", {"position": v(0, 0) * mm});
            skCircle(sketch, "E57.1.0", {"center": v(-67.78, -3.92) * mm, "radius": 1.5 * mm});
            skCircle(sketch, "E57.2.0", {"center": v(36.14, -58.73) * mm, "radius": 1.5 * mm});
            skCircle(sketch, "E58", {"center": v(-28, 60) * mm, "radius": 1.5 * mm});
            skCircle(sketch, "E59.1.0", {"center": v(-37.96, -54.25) * mm, "radius": 1.5 * mm});
            skCircle(sketch, "E59.2.0", {"center": v(65.96, -5.75) * mm, "radius": 1.5 * mm});
            skCircle(sketch, "E60.1.0", {"center": v(-65.96, -5.75) * mm, "radius": 1.5 * mm});
            skCircle(sketch, "E60.2.0", {"center": v(37.96, -54.25) * mm, "radius": 1.5 * mm});
            skSolve(sketch);
        }
        {
            var Q0;
            Q0=sQuery(id+"F46.wireOp",VERTEX,"E58.center");
            var Q1;
            Q1=sQuery(id+"F46.wireOp",VERTEX,"E55.center");
            var Q2;
            Q2=sQuery(id+"F46.wireOp",VERTEX,"E54.1.0.center");
            var Q3;
            Q3=sQuery(id+"F46.wireOp",VERTEX,"E59.2.0.center");
            var Q4;
            Q4=sQuery(id+"F46.wireOp",VERTEX,"E60.2.0.center");
            var Q5;
            Q5=sQuery(id+"F46.wireOp",VERTEX,"E53.center");
            var Q6;
            Q6=sQuery(id+"F46.wireOp",VERTEX,"E54.2.0.center");
            var Q7;
            Q7=sQuery(id+"F46.wireOp",VERTEX,"E59.1.0.center");
            var Q8;
            Q8=sQuery(id+"F46.wireOp",VERTEX,"E60.1.0.center");
            var Q9;
            Q9=makeQuery(id+"F15.opRevolve","SWEPT_BODY",BODY,{"disambiguationData":[OSD([sQuery(id+"F13.wireOp",EDGE,"E15.bottom"),sQuery(id+"F13.wireOp",EDGE,"E16.0"),sQuery(id+"F13.wireOp",EDGE,"E16.1"),sQuery(id+"F13.wireOp",EDGE,"E18"),sQuery(id+"F13.wireOp",EDGE,"E19")])]});
            var Q10;
            Q10=makeQuery(id+"F14.opRevolve","SWEPT_BODY",BODY,{"disambiguationData":[OSD([sQuery(id+"F13.wireOp",EDGE,"E15.top"),sQuery(id+"F13.wireOp",EDGE,"E15.right"),sQuery(id+"F13.wireOp",EDGE,"E16.1"),sQuery(id+"F13.wireOp",EDGE,"E16.2"),sQuery(id+"F13.wireOp",EDGE,"E17"),sQuery(id+"F13.wireOp",EDGE,"E19")])]});
            hole(context, id + "F47", {"style" : HoleStyle.C_BORE, "endStyle" : HoleEndStyle.BLIND, "holeDiameter" : 3 * mm, "cBoreDiameter" : 6 * mm, "cBoreDepth" : 2 * mm, "majorDiameter" : 5 * mm, "holeDepth" : 12 * mm, "isTappedThrough" : true, "tappedDepth" : 12 * mm, "tapClearance" : 3, "locations" : qUnion([Q0, Q1, Q2, Q3, Q4, Q5, Q6, Q7, Q8]), "scope" : qUnion([Q9, Q10])});
        }
        {
            var Q0;
            Q0=makeQuery(id+"F14.opRevolve","SWEPT_FACE",FACE,{"disambiguationData":[OSD([sQuery(id+"F13.wireOp",EDGE,"E15.top")])]});
            var sketch = newSketch(context, id + "F48", { "sketchPlane" : qUnion([Q0])});
            skLineSegment(sketch, "E61", {"start": v(0, 53) * mm, "end": v(0, 21) * mm, "construction": true});
            skLineSegment(sketch, "E62", {"start": v(0, 37) * mm, "end": v(-16.9, 51.17) * mm, "construction": true});
            skCircle(sketch, "E63", {"center": v(-13.79, 48.57) * mm, "radius": 1.4 * mm});
            skLineSegment(sketch, "E64", {"start": v(0, 37) * mm, "end": v(-3.8, 15.43) * mm, "construction": true});
            skLineSegment(sketch, "E65", {"start": v(0, 37) * mm, "end": v(31.8, 31.4) * mm, "construction": true});
            skCircle(sketch, "E66", {"center": v(-3.13, 19.27) * mm, "radius": 1.4 * mm});
            skCircle(sketch, "E67.1.0", {"center": v(-35.17, -36.23) * mm, "radius": 1.4 * mm});
            skCircle(sketch, "E67.2.0", {"center": v(48.96, -12.34) * mm, "radius": 1.4 * mm});
            skPoint(sketch, "E67.center", {"position": v(0, 0) * mm});
            skCircle(sketch, "E68.1.0", {"center": v(-15.13, -12.34) * mm, "radius": 1.4 * mm});
            skCircle(sketch, "E68.2.0", {"center": v(18.25, -6.93) * mm, "radius": 1.4 * mm});
            skCircle(sketch, "E69", {"center": v(18.71, 33.7) * mm, "radius": 1.4 * mm});
            skCircle(sketch, "E70.1.0", {"center": v(-38.54, -0.65) * mm, "radius": 1.4 * mm});
            skCircle(sketch, "E70.2.0", {"center": v(19.83, -33.05) * mm, "radius": 1.4 * mm});
            skLineSegment(sketch, "E71", {"start": v(0, 37) * mm, "end": v(-21.72, 11.12) * mm, "construction": true});
            skCircle(sketch, "E72", {"center": v(-12.21, 22.45) * mm, "radius": 1.4 * mm});
            skCircle(sketch, "E73.1.0", {"center": v(-13.33, -21.8) * mm, "radius": 1.4 * mm});
            skCircle(sketch, "E73.2.0", {"center": v(25.54, -0.65) * mm, "radius": 1.4 * mm});
            skSolve(sketch);
        }
        {
            var Q0;
            Q0 = qSketchRegion(id + "F48", true);
            extrude(context, id + "F49", {"entities" : qUnion([Q0]), "operationType" : NewBodyOperationType.REMOVE, "oppositeDirection" : true, "depth" : 2 * mm, "offsetDistance" : 25 * mm});
        }
        {
            var Q0;
            Q0=makeQuery(id+"F48.imprint","IMPRINT",FACE,{"disambiguationData":[TD([[makeQuery(id+"F48.imprint","IMPRINT",EDGE,{"derivedFrom":sQuery(id+"F48.wireOp",EDGE,"E70.1.0")}),1.0]])]});
            var Q1;
            Q1=makeQuery(id+"F48.imprint","IMPRINT",FACE,{"disambiguationData":[TD([[makeQuery(id+"F48.imprint","IMPRINT",EDGE,{"derivedFrom":sQuery(id+"F48.wireOp",EDGE,"E73.1.0")}),1.0]])]});
            var Q2;
            Q2=makeQuery(id+"F48.imprint","IMPRINT",FACE,{"disambiguationData":[TD([[makeQuery(id+"F48.imprint","IMPRINT",EDGE,{"derivedFrom":sQuery(id+"F48.wireOp",EDGE,"E70.2.0")}),1.0]])]});
            var Q3;
            Q3=makeQuery(id+"F48.imprint","IMPRINT",FACE,{"disambiguationData":[TD([[makeQuery(id+"F48.imprint","IMPRINT",EDGE,{"derivedFrom":sQuery(id+"F48.wireOp",EDGE,"E73.2.0")}),1.0]])]});
            var Q4;
            Q4=makeQuery(id+"F48.imprint","IMPRINT",FACE,{"disambiguationData":[TD([[makeQuery(id+"F48.imprint","IMPRINT",EDGE,{"derivedFrom":sQuery(id+"F48.wireOp",EDGE,"E69")}),1.0]])]});
            var Q5;
            Q5=makeQuery(id+"F48.imprint","IMPRINT",FACE,{"disambiguationData":[TD([[makeQuery(id+"F48.imprint","IMPRINT",EDGE,{"derivedFrom":sQuery(id+"F48.wireOp",EDGE,"E72")}),1.0]])]});
            var Q6;
            Q6=sQuery(id+"F48.wireOp",EDGE,"E69");
            var Q7;
            Q7=sQuery(id+"F48.wireOp",EDGE,"E72");
            var Q8;
            Q8=sQuery(id+"F48.wireOp",EDGE,"E70.1.0");
            var Q9;
            Q9=sQuery(id+"F48.wireOp",EDGE,"E73.1.0");
            var Q10;
            Q10=sQuery(id+"F48.wireOp",EDGE,"E70.2.0");
            var Q11;
            Q11=sQuery(id+"F48.wireOp",EDGE,"E73.2.0");
            extrude(context, id + "F50", {"entities" : qUnion([Q0, Q1, Q2, Q3, Q4, Q5]), "operationType" : NewBodyOperationType.REMOVE, "surfaceEntities" : qUnion([Q6, Q7, Q8, Q9, Q10, Q11]), "depth" : 44 * mm, "offsetDistance" : 25 * mm});
        }
        {
            var Q0;
            {var subQ0=sQuery(id+"F32.wireOp",EDGE,"E41.right");var subQ1=sQuery(id+"F32.wireOp",EDGE,"E41.left");var subQ2=sQuery(id+"F32.wireOp",EDGE,"E41.top");var subQ3=sQuery(id+"F32.wireOp",EDGE,"E41.bottom");var subQ4=makeQuery(id+"F33.opRevolve","CAP_FACE",FACE,{"disambiguationData":[OSD([subQ3,subQ2,subQ1,subQ0])],"isStart":false});var subQ5=sQuery(id+"F13.wireOp",EDGE,"E16.2");var subQ6=makeQuery(id+"F14.opRevolve","SWEPT_FACE",FACE,{"disambiguationData":[OSD([subQ5])]});Q0=makeQuery(id+"F37.boolean.opBoolean","MERGE",FACE,{"derivedFrom":[makeQuery(id+"F33.boolean.opBoolean","COPY",FACE,{"disambiguationData":[TD([makeQuery(id+"F14.opRevolve","SWEPT_FACE",FACE,{"disambiguationData":[OSD([sQuery(id+"F13.wireOp",EDGE,"E15.top")])]})])],"derivedFrom":subQ4}),makeQuery(id+"F37.opExtrude","SWEPT_FACE",FACE,{"disambiguationData":[OSD([subQ5,subQ3,subQ2,subQ1,subQ0]),TDD([makeQuery(id+"F36.imprint","IMPRINT",EDGE,{"derivedFrom":makeQuery(id+"F33.boolean.opBoolean","INTERSECT",EDGE,{"derivedFrom":[subQ6,subQ4]})})])]})]});}
            var sketch = newSketch(context, id + "F51", { "sketchPlane" : qUnion([Q0])});
            skLineSegment(sketch, "E74.bottom", {"start": v(57.67, -11) * mm, "end": v(22, -11) * mm});
            skLineSegment(sketch, "E74.top", {"start": v(57.67, 1) * mm, "end": v(22, 1) * mm});
            skLineSegment(sketch, "E74.left", {"start": v(57.67, -11) * mm, "end": v(57.67, 1) * mm});
            skLineSegment(sketch, "E74.right", {"start": v(22, -11) * mm, "end": v(22, 1) * mm});
            skPoint(sketch, "E74.middle.positionSnap0", {"position": v(20, -1) * mm});
            skPoint(sketch, "E74.centerSnap0", {"position": v(20, -1) * mm});
            skSolve(sketch);
        }
        {
            var Q0;
            Q0=makeQuery(id+"F51.imprint","IMPRINT",FACE,{"disambiguationData":[TD([[makeQuery(id+"F51.imprint","IMPRINT",EDGE,{"derivedFrom":sQuery(id+"F51.wireOp",EDGE,"E74.bottom")}),-1.0]])]});
            extrude(context, id + "F52", {"entities" : qUnion([Q0]), "operationType" : NewBodyOperationType.REMOVE, "oppositeDirection" : true, "depth" : 25 * mm, "offsetDistance" : 25 * mm});
        }
        {
            var Q0;
            {var subQ0=sQuery(id+"F28.wireOp",EDGE,"E40.right");var subQ1=sQuery(id+"F28.wireOp",EDGE,"E40.left");var subQ2=sQuery(id+"F28.wireOp",EDGE,"E40.top");var subQ3=sQuery(id+"F28.wireOp",EDGE,"E40.bottom");var subQ4=makeQuery(id+"F29.opRevolve","CAP_FACE",FACE,{"disambiguationData":[OSD([subQ3,subQ2,subQ1,subQ0])],"isStart":false});var subQ5=sQuery(id+"F13.wireOp",EDGE,"E16.2");var subQ6=makeQuery(id+"F14.opRevolve","SWEPT_FACE",FACE,{"disambiguationData":[OSD([subQ5])]});Q0=makeQuery(id+"F37.boolean.opBoolean","MERGE",FACE,{"derivedFrom":[makeQuery(id+"F29.boolean.opBoolean","COPY",FACE,{"disambiguationData":[TD([makeQuery(id+"F14.opRevolve","SWEPT_FACE",FACE,{"disambiguationData":[OSD([sQuery(id+"F13.wireOp",EDGE,"E15.top")])]})])],"derivedFrom":subQ4}),makeQuery(id+"F37.opExtrude","SWEPT_FACE",FACE,{"disambiguationData":[OSD([subQ5,subQ3,subQ2,subQ1,subQ0]),TDD([makeQuery(id+"F36.imprint","IMPRINT",EDGE,{"derivedFrom":makeQuery(id+"F29.boolean.opBoolean","INTERSECT",EDGE,{"derivedFrom":[subQ6,subQ4]})})])]})]});}
            var sketch = newSketch(context, id + "F53", { "sketchPlane" : qUnion([Q0])});
            skLineSegment(sketch, "E75.bottom", {"start": v(58.2, -10) * mm, "end": v(23.5, -10) * mm});
            skLineSegment(sketch, "E75.top", {"start": v(58.2, 2) * mm, "end": v(23.5, 2) * mm});
            skLineSegment(sketch, "E75.left", {"start": v(58.2, -10) * mm, "end": v(58.2, 2) * mm});
            skLineSegment(sketch, "E75.right", {"start": v(23.5, -10) * mm, "end": v(23.5, 2) * mm});
            skSolve(sketch);
        }
        {
            var Q0;
            Q0=makeQuery(id+"F53.imprint","IMPRINT",FACE,{"disambiguationData":[TD([[makeQuery(id+"F53.imprint","IMPRINT",EDGE,{"derivedFrom":sQuery(id+"F53.wireOp",EDGE,"E75.bottom")}),-1.0]])]});
            extrude(context, id + "F54", {"entities" : qUnion([Q0]), "operationType" : NewBodyOperationType.REMOVE, "oppositeDirection" : true, "depth" : 25 * mm, "offsetDistance" : 25 * mm});
        }
        {
            var Q0;
            {var subQ0=sQuery(id+"F34.wireOp",EDGE,"E42.right");var subQ1=sQuery(id+"F34.wireOp",EDGE,"E42.left");var subQ2=sQuery(id+"F34.wireOp",EDGE,"E42.top");var subQ3=sQuery(id+"F34.wireOp",EDGE,"E42.bottom");var subQ4=makeQuery(id+"F35.opRevolve","CAP_FACE",FACE,{"disambiguationData":[OSD([subQ3,subQ2,subQ1,subQ0])],"isStart":false});var subQ5=sQuery(id+"F13.wireOp",EDGE,"E16.2");var subQ6=makeQuery(id+"F14.opRevolve","SWEPT_FACE",FACE,{"disambiguationData":[OSD([subQ5])]});Q0=makeQuery(id+"F37.boolean.opBoolean","MERGE",FACE,{"derivedFrom":[makeQuery(id+"F35.boolean.opBoolean","COPY",FACE,{"disambiguationData":[TD([makeQuery(id+"F14.opRevolve","SWEPT_FACE",FACE,{"disambiguationData":[OSD([sQuery(id+"F13.wireOp",EDGE,"E15.top")])]})])],"derivedFrom":subQ4}),makeQuery(id+"F37.opExtrude","SWEPT_FACE",FACE,{"disambiguationData":[OSD([subQ5,subQ3,subQ2,subQ1,subQ0]),TDD([makeQuery(id+"F36.imprint","IMPRINT",EDGE,{"derivedFrom":makeQuery(id+"F35.boolean.opBoolean","INTERSECT",EDGE,{"derivedFrom":[subQ6,subQ4]})})])]})]});}
            var sketch = newSketch(context, id + "F55", { "sketchPlane" : qUnion([Q0])});
            skLineSegment(sketch, "E76.bottom", {"start": v(57.67, -11) * mm, "end": v(22, -11) * mm});
            skLineSegment(sketch, "E76.top", {"start": v(57.67, 1) * mm, "end": v(22, 1) * mm});
            skLineSegment(sketch, "E76.left", {"start": v(57.67, -11) * mm, "end": v(57.67, 1) * mm});
            skLineSegment(sketch, "E76.right", {"start": v(22, -11) * mm, "end": v(22, 1) * mm});
            skPoint(sketch, "E76.middle.positionSnap0", {"position": v(59.67, -1) * mm});
            skPoint(sketch, "E76.centerSnap0", {"position": v(59.67, -1) * mm});
            skSolve(sketch);
        }
        {
            var Q0;
            Q0 = qSketchRegion(id + "F55", true);
            extrude(context, id + "F56", {"entities" : qUnion([Q0]), "operationType" : NewBodyOperationType.REMOVE, "oppositeDirection" : true, "depth" : 25 * mm, "offsetDistance" : 25 * mm});
        }
        {
            var Q0;
            Q0=makeQuery(id+"F3.imprint","IMPRINT",FACE,{"disambiguationData":[TD([[makeQuery(id+"F3.imprint","IMPRINT",EDGE,{"derivedFrom":sQuery(id+"F3.wireOp",EDGE,"E6")}),1.0]])]});
            var Q1;
            {var subQ0=sQuery(id+"F3.wireOp",EDGE,"E5");var subQ1=makeQuery(id+"F1.opExtrude","CAP_EDGE",EDGE,{"disambiguationData":[OSD([sQuery(id+"F0.wireOp",EDGE,"E1.1")])],"isStart":false});var subQ2=makeQuery(id+"F3.imprint","INTERSECT",VERTEX,{"disambiguationData":[OD(0.0)],"derivedFrom":[subQ1,subQ0]});Q1=makeQuery(id+"F3.imprint","IMPRINT",FACE,{"disambiguationData":[TD([[makeQuery(id+"F3.imprint","IMPRINT",EDGE,{"disambiguationData":[TD([[subQ2,-1.0]])],"derivedFrom":subQ0}),1.0]])]});}
            extrude(context, id + "F57", {"entities" : qUnion([Q0, Q1]), "operationType" : NewBodyOperationType.REMOVE, "oppositeDirection" : true, "depth" : 2 * mm, "offsetDistance" : 25 * mm});
        }
        {
            var Q0;
            {var subQ0=sQuery(id+"F4.wireOp",EDGE,"E9");var subQ1=makeQuery(id+"F1.opExtrude","CAP_EDGE",EDGE,{"disambiguationData":[OSD([sQuery(id+"F0.wireOp",EDGE,"E1.2")])],"isStart":false});var subQ2=makeQuery(id+"F4.imprint","INTERSECT",VERTEX,{"disambiguationData":[OD(0.0)],"derivedFrom":[subQ1,subQ0]});Q0=makeQuery(id+"F4.imprint","IMPRINT",FACE,{"disambiguationData":[TD([[makeQuery(id+"F4.imprint","IMPRINT",EDGE,{"disambiguationData":[TD([[subQ2,1.0]])],"derivedFrom":subQ0}),1.0]])]});}
            var Q1;
            Q1=makeQuery(id+"F4.imprint","IMPRINT",FACE,{"disambiguationData":[TD([[makeQuery(id+"F4.imprint","IMPRINT",EDGE,{"derivedFrom":sQuery(id+"F4.wireOp",EDGE,"E10")}),1.0]])]});
            extrude(context, id + "F58", {"entities" : qUnion([Q0, Q1]), "operationType" : NewBodyOperationType.REMOVE, "oppositeDirection" : true, "depth" : 2 * mm, "offsetDistance" : 25 * mm});
        }
        {
            var Q0;
            {var subQ0=sQuery(id+"F5.wireOp",EDGE,"E13");var subQ1=makeQuery(id+"F1.opExtrude","CAP_EDGE",EDGE,{"disambiguationData":[OSD([sQuery(id+"F0.wireOp",EDGE,"E1.0")])],"isStart":false});var subQ2=makeQuery(id+"F5.imprint","INTERSECT",VERTEX,{"disambiguationData":[OD(0.0)],"derivedFrom":[subQ1,subQ0]});Q0=makeQuery(id+"F5.imprint","IMPRINT",FACE,{"disambiguationData":[TD([[makeQuery(id+"F5.imprint","IMPRINT",EDGE,{"disambiguationData":[TD([[subQ2,1.0]])],"derivedFrom":subQ0}),1.0]])]});}
            var Q1;
            Q1=makeQuery(id+"F5.imprint","IMPRINT",FACE,{"disambiguationData":[TD([[makeQuery(id+"F5.imprint","IMPRINT",EDGE,{"derivedFrom":sQuery(id+"F5.wireOp",EDGE,"E14")}),1.0]])]});
            extrude(context, id + "F59", {"entities" : qUnion([Q0, Q1]), "operationType" : NewBodyOperationType.REMOVE, "oppositeDirection" : true, "depth" : 2 * mm, "offsetDistance" : 25 * mm});
        }
    });
